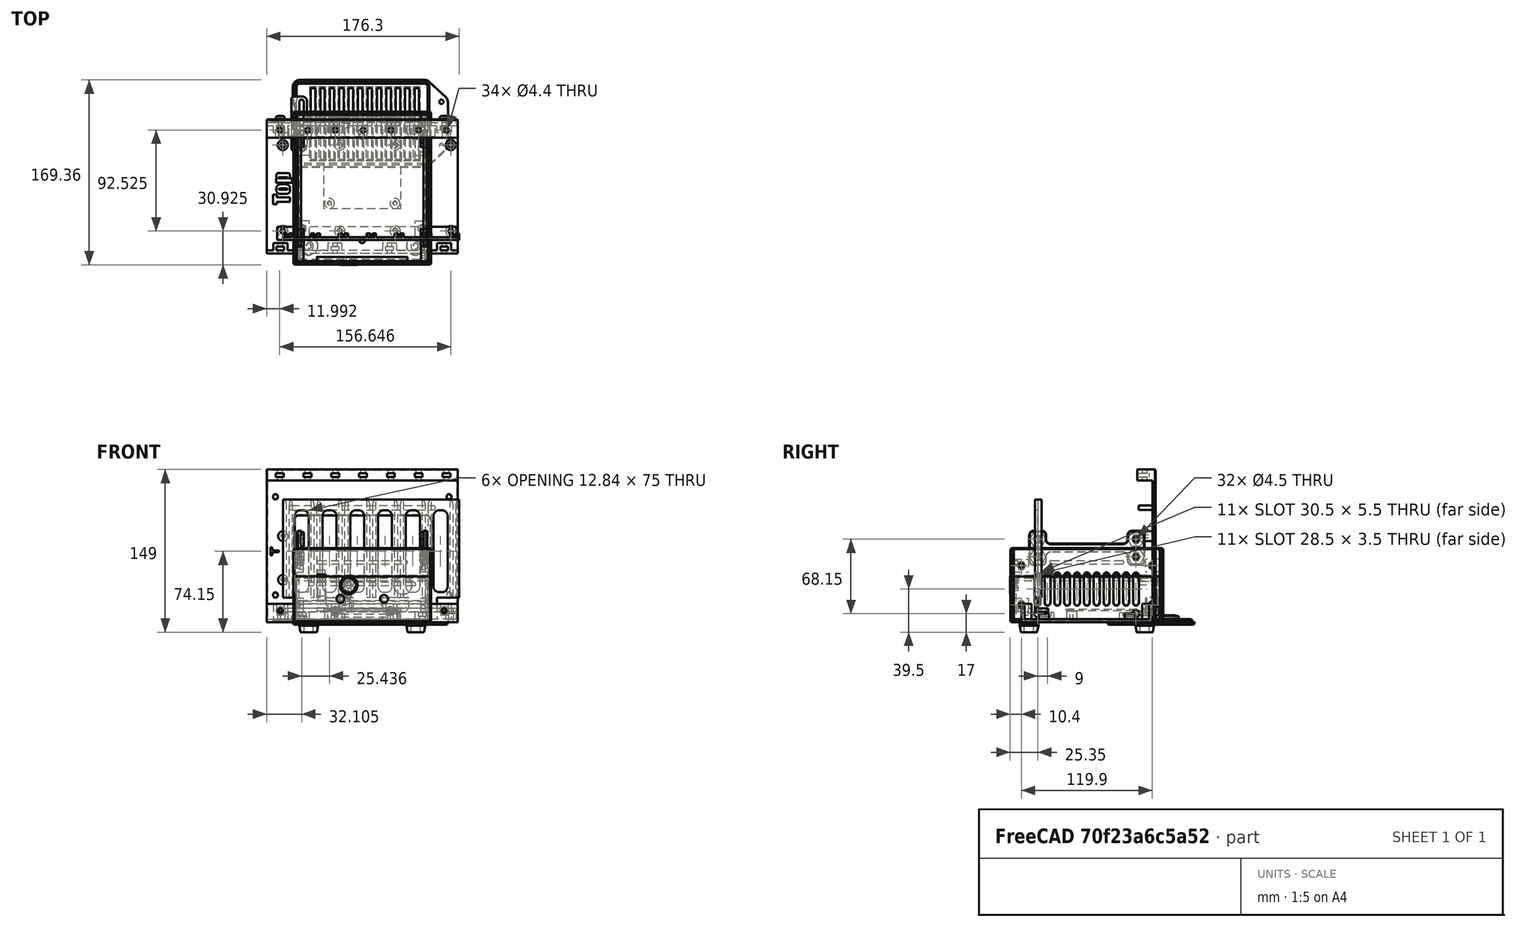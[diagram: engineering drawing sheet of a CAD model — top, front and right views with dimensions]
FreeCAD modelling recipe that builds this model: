
FCSTD DOCUMENT  (FreeCAD 0.19R14555 (Git shallow))
Label: Assembly Model
License: All rights reserved
LicenseURL: http://en.wikipedia.org/wiki/All_rights_reserved
objects: Sketcher::SketchObject×46, PartDesign::Pocket×26, PartDesign::Chamfer×23, PartDesign::Pad×20, PartDesign::Mirrored×12, PartDesign::Body×10, Part::Feature×8, Part::FeaturePython×5, App::Part×5, Part::Mirroring×4, App::DocumentObjectGroup×4, PartDesign::Fillet×4, PartDesign::LinearPattern×1, PartDesign::Revolution×1, PartDesign::Thickness×1, Part::Part2DObjectPython×1
note: 237 computed .brp shape members not serialized (recipe doc carries the construction recipe); baked Part::Feature solids carry a one-line shape summary decoded from their .brp

FEATURE [Part::Feature] Part__Feature001  label="Guide"
  Placement = pos=(4.1875,39.425,9.65) rot=(0,0,1;0rad)
  shape: bbox 166.6 x 12 x 103 mm, 167 faces (baked)
FEATURE [Part::Mirroring] Part__Mirroring001  label="Guide (Mirror #2)"
  Base = (0,0,0)
  Normal = (0,1,0)
  Source = -> Part__Feature001
FEATURE [Part::Feature] Part__Feature004  label="M4 X 10 Pan Hd Pozi"
  Placement = pos=(-75,-63.15,10.5) rot=(1,0,0;1.5708rad)
  shape: bbox 8.444 x 13.1 x 8.444 mm, 27 faces (baked)
FEATURE [Part::FeaturePython] Array  # Draft array (typed FeaturePython)
  Angle = 360
  ArrayType = 0
  Axis = (0,0,1)
  Base = -> Part__Feature004
  Center = (0,0,0)
  Fuse = false
  IntervalAxis = (0,0,0)
  IntervalX = (50,0,0)
  IntervalY = (0,1,0)
  IntervalZ = (0,0,1)
  NumberPolar = 1
  NumberX = 4
  NumberY = 1
  NumberZ = 1
FEATURE [Part::Mirroring] Part__Mirroring003  label="Side panel retaining nuts"
  Base = (0,0,0)
  Normal = (0,1,0)
  Source = -> Array
FEATURE [Part::Feature] Part__Feature005  label="M4 Nut"
  Placement = pos=(-75,-55.375,10.5) rot=(1,0,0;0rad)
  shape: bbox 7.66 x 3.2 x 7.66 mm, 19 faces (baked)
FEATURE [Part::Feature] Part__Feature006  label="Sideplate"
  Placement = pos=(-8e-15,-63.1,0) rot=(0,0.707107,0.707107;3.14159rad)
  shape: bbox 175 x 17 x 140 mm, 120 faces (baked)
FEATURE [Part::Mirroring] Part__Mirroring  label="Sideplate (Mirror #5)"
  Base = (0,0,0)
  Normal = (0,1,0)
  Source = -> Part__Feature006
FEATURE [Part::Feature] Part__Feature007  label="Vented_cover"
  shape: bbox 142 x 80.02 x 8.7 mm, 193 faces (baked)
FEATURE [Part::Feature] Part__Feature008  label="Tab"
  shape: bbox 14.5 x 50 x 2.7 mm, 17 faces (baked)
FEATURE [App::DocumentObjectGroup] Group  label="Side-cover assy"
  Group = -> [Part__Feature007,Part__Feature008]
FEATURE [App::Part] Part  label="Side Cover Assy"
  Group = -> [Part__Feature008,Part__Feature007,Group]
  Origin = -> Origin002
  Placement = pos=(-7.7e-15,-63,0) rot=(0,0.707107,0.707107;3.14159rad)
FEATURE [Part::Feature] Part__Feature009  label="Tab001"
  shape: bbox 14.5 x 50 x 2.7 mm, 17 faces (baked)
FEATURE [Part::Feature] Part__Feature010  label="Vented_cover001"
  shape: bbox 142 x 80.02 x 8.7 mm, 193 faces (baked)
FEATURE [App::DocumentObjectGroup] Group001  label="Side-cover assy001"
  Group = -> [Part__Feature010,Part__Feature009]
FEATURE [App::Part] Part001  label="Side Cover Assy 2"
  Group = -> [Part__Feature009,Part__Feature010,Group001]
  Origin = -> Origin003
  Placement = pos=(7.7e-15,63,118) rot=(0,0.707107,-0.707107;3.14159rad)
FEATURE [Part::FeaturePython] Array001  label="Nuts for sideplate"  # Draft array (typed FeaturePython)
  Angle = 360
  ArrayType = 0
  Axis = (0,0,1)
  Base = -> Part__Feature005
  Center = (0,0,0)
  Fuse = false
  IntervalAxis = (0,0,0)
  IntervalX = (50,0,0)
  IntervalY = (0,1,0)
  IntervalZ = (0,0,1)
  NumberPolar = 1
  NumberX = 4
  NumberY = 1
  NumberZ = 1
FEATURE [Part::Mirroring] Part__Mirroring004  label="Nuts for sideplate (Mirror #5)"
  Base = (0,0,0)
  Normal = (0,1,0)
  Source = -> Array001
FEATURE [Sketcher::SketchObject] Sketch001  label="Base plate spec"
  FullyConstrained = false
  MapMode = 5
  Support = -> [XY_Plane005]
  sketch-geometry (12):
    g0: LineSegment StartX=-63 StartY=67 StartZ=0 EndX=63 EndY=67 EndZ=0
    g1: LineSegment StartX=63 StartY=67 StartZ=0 EndX=63 EndY=-67 EndZ=0
    g2: LineSegment StartX=63 StartY=-67 StartZ=0 EndX=-63 EndY=-67 EndZ=0
    g3: LineSegment StartX=-63 StartY=-67 StartZ=0 EndX=-63 EndY=67 EndZ=0
    g4: Circle CenterX=-49 CenterY=53 CenterZ=0 NormalX=0 NormalY=0 NormalZ=1 AngleXU=0 Radius=2.4
    g5: Circle CenterX=49 CenterY=53 CenterZ=0 NormalX=0 NormalY=0 NormalZ=1 AngleXU=0 Radius=2.4
    g6: Circle CenterX=-49 CenterY=-53 CenterZ=0 NormalX=0 NormalY=0 NormalZ=1 AngleXU=0 Radius=2.4
    g7: Circle CenterX=49 CenterY=-53 CenterZ=0 NormalX=0 NormalY=0 NormalZ=1 AngleXU=0 Radius=2.4
    g8: Circle CenterX=55 CenterY=37 CenterZ=0 NormalX=0 NormalY=0 NormalZ=1 AngleXU=0 Radius=2.4
    g9: Circle CenterX=-55 CenterY=37 CenterZ=0 NormalX=0 NormalY=0 NormalZ=1 AngleXU=0 Radius=2.4
    g10: Circle CenterX=-55 CenterY=-37 CenterZ=0 NormalX=0 NormalY=0 NormalZ=1 AngleXU=0 Radius=2.4
    g11: Circle CenterX=55 CenterY=-37 CenterZ=0 NormalX=0 NormalY=0 NormalZ=1 AngleXU=0 Radius=2.4
  constraints (28):
    c: Coincident(g0,g1)
    c: Coincident(g1,g2)
    c: Coincident(g2,g3)
    c: Coincident(g3,g0)
    c: Horizontal(g2)
    c: Vertical(g1)
    c: Symmetric(g0,g0,g-2)
    c: Symmetric(g0,g2,g-1)
    c: Distance(g0) = 126
    c: Distance(g3) = 134
    c: Radius(g4) = 2.4
    c: Equal(g4,g5)
    c: Equal(g4,g6)
    c: Equal(g4,g7)
    c: Symmetric(g4,g5,g-2)
    c: Symmetric(g4,g6,g-1)
    c: Symmetric(g7,g6,g-2)
    c: Distance(g4,g5) = 98
    c: DistanceY(g6,g4) = 106
    c: Symmetric(g10,g11,g-2)
    c: Symmetric(g9,g10,g-1)
    c: Symmetric(g9,g8,g-2)
    c: Radius(g9) = 2.4
    c: Equal(g9,g8)
    c: Equal(g9,g11)
    c: Equal(g9,g10)
    c: DistanceX(g0,g9) = 8
    c: DistanceY(g9,g0) = 30
FEATURE [PartDesign::Pad] Pad  label="Make base plate"
  AllowMultiFace = false
  Direction = (1,1,1)
  Length = 3
  Length2 = 100
  Profile = -> Sketch001
  Type = 0
FEATURE [Sketcher::SketchObject] Sketch002  label="Sideplate spec"
  FullyConstrained = false
  MapMode = 5
  Placement = pos=(0,0,0) rot=(1,0,0;1.5708rad)
  Support = -> [XZ_Plane006]
  sketch-geometry (4):
    g0: LineSegment StartX=-60 StartY=3.05 StartZ=0 EndX=-63 EndY=3.05 EndZ=0
    g1: LineSegment StartX=-63 StartY=3.05 StartZ=0 EndX=-63 EndY=68.05 EndZ=0
    g2: LineSegment StartX=-63 StartY=68.05 StartZ=0 EndX=-60 EndY=68.05 EndZ=0
    g3: LineSegment StartX=-60 StartY=68.05 StartZ=0 EndX=-60 EndY=3.05 EndZ=0
  constraints (12):
    c: Coincident(g0,g1)
    c: Coincident(g1,g2)
    c: Coincident(g2,g3)
    c: Horizontal(g0)
    c: Horizontal(g2)
    c: Vertical(g3)
    c: Vertical(g1)
    c: Distance(g1) = 65
    c: Distance(g2) = 3
    c: DistanceX(g0) = -63
    c: DistanceY(g0) = 3.05
    c: Coincident(g3,g0)
FEATURE [PartDesign::Pad] Pad001  label="Make sideplate"
  AllowMultiFace = false
  Direction = (1,1,1)
  Length = 134
  Length2 = 100
  Midplane = true
  Placement = pos=(0,0,0) rot=(1,0,0;1.5708rad)
  Profile = -> Sketch002
  Type = 0
FEATURE [Sketcher::SketchObject] Sketch003  label="Screwtab spec"
  ExternalGeometry = -> [Pad001]
  FullyConstrained = false
  MapMode = 5
  Placement = pos=(0,0,3.05) rot=(1,0,0;3.14159rad)
  Support = -> [Pad001]
  sketch-geometry (13):
    g0: LineSegment StartX=-60 StartY=44 StartZ=0 EndX=-48.5 EndY=44 EndZ=0
    g1: LineSegment StartX=-48.5 StartY=44 StartZ=0 EndX=-48.5 EndY=30 EndZ=0
    g2: LineSegment StartX=-48.5 StartY=30 StartZ=0 EndX=-60 EndY=30 EndZ=0
    g3: LineSegment StartX=-60 StartY=30 StartZ=0 EndX=-60 EndY=44 EndZ=0
    g4: LineSegment StartX=-60 StartY=37 StartZ=0 EndX=-48.5 EndY=37 EndZ=0
    g5: Circle CenterX=-55 CenterY=37 CenterZ=0 NormalX=0 NormalY=0 NormalZ=1 AngleXU=0 Radius=2.4
    g6: LineSegment StartX=-51.5 StartY=34.9793 StartZ=0 EndX=-51.5 EndY=39.0207 EndZ=0
    g7: LineSegment StartX=-51.5 StartY=39.0207 StartZ=0 EndX=-55 EndY=41.0415 EndZ=0
    g8: LineSegment StartX=-55 StartY=41.0415 StartZ=0 EndX=-58.5 EndY=39.0207 EndZ=0
    g9: LineSegment StartX=-58.5 StartY=39.0207 StartZ=0 EndX=-58.5 EndY=34.9793 EndZ=0
    g10: LineSegment StartX=-58.5 StartY=34.9793 StartZ=0 EndX=-55 EndY=32.9585 EndZ=0
    g11: LineSegment StartX=-55 StartY=32.9585 StartZ=0 EndX=-51.5 EndY=34.9793 EndZ=0
    g12: Circle CenterX=-55 CenterY=37 CenterZ=0 NormalX=0 NormalY=0 NormalZ=1 AngleXU=0 Radius=4.04145
  constraints (34):
    c: Coincident(g0,g1)
    c: Coincident(g1,g2)
    c: Coincident(g2,g3)
    c: Coincident(g3,g0)
    c: Horizontal(g0)
    c: Horizontal(g2)
    c: Vertical(g1)
    c: Vertical(g3)
    c: Perpendicular(g4,g1) = 4.71239
    c: PointOnObject(g4,g3)
    c: PointOnObject(g5,g4)
    c: PointOnObject(g0,g-3)
    c: Symmetric(g0,g1,g4)
    c: DistanceY(g5,g-3) = 30
    c: DistanceX(g-4,g5) = 8
    c: Coincident(g6,g7)
    c: Coincident(g7,g8)
    c: Coincident(g8,g9)
    c: Coincident(g9,g10)
    c: Coincident(g10,g11)
    c: Coincident(g11,g6)
    c: Equal(g6, g7-g11) x5
    c: PointOnObject(g6,g12)
    c: PointOnObject(g7,g12)
    c: PointOnObject(g8,g12)
    c: PointOnObject(g9,g12)
    c: PointOnObject(g10,g12)
    c: PointOnObject(g11,g12)
    c: Coincident(g12,g5)
    c: Vertical(g6)
    c: DistanceX(g9,g6) = 7
    c: DistanceX(g6,g0) = 3
    c: Distance(g1) = 14
    c: Radius(g5) = 2.4
FEATURE [PartDesign::Pad] Pad002  label="Add screwtab"
  AllowMultiFace = false
  BaseFeature = -> Pad001
  Direction = (1,1,1)
  Length = 6
  Length2 = 100
  Placement = pos=(0,0,0) rot=(1,0,0;1.5708rad)
  Profile = -> Sketch003
  Reversed = true
  Type = 0
FEATURE [PartDesign::Mirrored] Mirrored  label="Mirrored screwtab"
  BaseFeature = -> Pad002
  MirrorPlane = -> XZ_Plane006
  Originals = -> [Pad002]
  Placement = pos=(0,0,0) rot=(1,0,0;1.5708rad)
FEATURE [Sketcher::SketchObject] Sketch004  label="nut trap spec"
  ExternalGeometry = -> [Mirrored]
  FullyConstrained = false
  MapMode = 5
  Placement = pos=(0,-2e-15,9.05) rot=(0,0,1;3.14159rad)
  Support = -> [Mirrored]
  sketch-geometry (7):
    g0: LineSegment StartX=58.55 StartY=34.9504 StartZ=0 EndX=58.55 EndY=39.0496 EndZ=0
    g1: LineSegment StartX=58.55 StartY=39.0496 StartZ=0 EndX=55 EndY=41.0992 EndZ=0
    g2: LineSegment StartX=55 StartY=41.0992 StartZ=0 EndX=51.45 EndY=39.0496 EndZ=0
    g3: LineSegment StartX=51.45 StartY=39.0496 StartZ=0 EndX=51.45 EndY=34.9504 EndZ=0
    g4: LineSegment StartX=51.45 StartY=34.9504 StartZ=0 EndX=55 EndY=32.9008 EndZ=0
    g5: LineSegment StartX=55 StartY=32.9008 StartZ=0 EndX=58.55 EndY=34.9504 EndZ=0
    g6: Circle CenterX=55 CenterY=37 CenterZ=0 NormalX=0 NormalY=0 NormalZ=1 AngleXU=0 Radius=4.09919
  constraints (16):
    c: Coincident(g0,g1)
    c: Coincident(g1,g2)
    c: Coincident(g2,g3)
    c: Coincident(g3,g4)
    c: Coincident(g4,g5)
    c: Coincident(g5,g0)
    c: Equal(g0, g1-g5) x5
    c: PointOnObject(g0,g6)
    c: PointOnObject(g1,g6)
    c: PointOnObject(g2,g6)
    c: PointOnObject(g3,g6)
    c: PointOnObject(g4,g6)
    c: PointOnObject(g5,g6)
    c: Coincident(g6,g-3)
    c: Vertical(g0)
    c: Distance(g0,g3) = 7.1
FEATURE [PartDesign::Pocket] Pocket  label="Add nut trap"
  AllowMultiFace = false
  BaseFeature = -> Mirrored
  Length = 3.5
  Length2 = 100
  Placement = pos=(0,0,0) rot=(1,0,0;1.5708rad)
  Profile = -> Sketch004
  Type = 0
FEATURE [PartDesign::Mirrored] Mirrored001  label="Mirrored nut-trap"
  BaseFeature = -> Pocket
  MirrorPlane = -> XZ_Plane006
  Originals = -> [Pocket]
  Placement = pos=(0,0,0) rot=(1,0,0;1.5708rad)
FEATURE [Sketcher::SketchObject] Sketch005  label="PCB Base"
  FullyConstrained = false
  MapMode = 5
  Support = -> [XY_Plane007]
  sketch-geometry (11):
    g0: LineSegment StartX=-50 StartY=35 StartZ=0 EndX=35 EndY=35 EndZ=0
    g1: LineSegment StartX=35 StartY=35 StartZ=0 EndX=35 EndY=-35 EndZ=0
    g2: LineSegment StartX=35 StartY=-35 StartZ=0 EndX=-50 EndY=-35 EndZ=0
    g3: LineSegment StartX=-50 StartY=-35 StartZ=0 EndX=-50 EndY=35 EndZ=0
    g4: Circle CenterX=-45 CenterY=-30 CenterZ=0 NormalX=0 NormalY=0 NormalZ=1 AngleXU=0 Radius=2.1
    g5: Circle CenterX=30 CenterY=-30 CenterZ=0 NormalX=0 NormalY=0 NormalZ=1 AngleXU=0 Radius=2.1
    g6: Circle CenterX=-45 CenterY=30 CenterZ=0 NormalX=0 NormalY=0 NormalZ=1 AngleXU=0 Radius=2.1
    g7: Circle CenterX=30 CenterY=30 CenterZ=0 NormalX=0 NormalY=0 NormalZ=1 AngleXU=0 Radius=2.1
    g8: LineSegment StartX=-7.5 StartY=35 StartZ=0 EndX=-7.5 EndY=-35 EndZ=0
    g9: LineSegment StartX=-50 StartY=-3.1e-15 StartZ=0 EndX=35 EndY=2.1e-15 EndZ=0
    g10: GeomPoint X=0 Y=0 Z=0
  constraints (28):
    c: Coincident(g0,g1)
    c: Coincident(g1,g2)
    c: Coincident(g2,g3)
    c: Coincident(g3,g0)
    c: Horizontal(g0)
    c: Horizontal(g2)
    c: Vertical(g1)
    c: Vertical(g3)
    c: Distance(g3) = 70
    c: Distance(g0) = 85
    c: Radius(g6) = 2.1
    c: Equal(g6,g7)
    c: Equal(g6,g4)
    c: Equal(g6,g5)
    c: Perpendicular(g9,g3) = 1.5708
    c: Perpendicular(g8,g0) = 1.5708
    c: PointOnObject(g8,g2)
    c: PointOnObject(g9,g1)
    c: Symmetric(g2,g0,g9)
    c: Symmetric(g0,g0,g8)
    c: Symmetric(g6,g7,g8)
    c: Symmetric(g4,g6,g9)
    c: Symmetric(g4,g5,g8)
    c: DistanceX(g2,g4) = 5
    c: DistanceY(g2,g4) = 5
    c: Coincident(g10,g-1)
    c: PointOnObject(g10,g9)
    c: DistanceX(g0) = 35
FEATURE [PartDesign::Pad] Pad003  label="Make PCB Laminate"
  AllowMultiFace = false
  Direction = (1,1,1)
  Length = 1.6
  Length2 = 100
  Profile = -> Sketch005
  Type = 0
FEATURE [Sketcher::SketchObject] Sketch006  label="DCJack footprint"
  ExternalGeometry = -> [Pad003]
  FullyConstrained = false
  MapMode = 5
  Placement = pos=(0,0,1.6) rot=(0,0,1;0rad)
  Support = -> [Pad003]
  sketch-geometry (7):
    g0: LineSegment StartX=23.95 StartY=20.45 StartZ=0 EndX=38 EndY=20.45 EndZ=0
    g1: LineSegment StartX=38 StartY=20.45 StartZ=0 EndX=38 EndY=11.45 EndZ=0
    g2: LineSegment StartX=38 StartY=11.45 StartZ=0 EndX=23.95 EndY=11.45 EndZ=0
    g3: LineSegment StartX=23.95 StartY=11.45 StartZ=0 EndX=23.95 EndY=20.45 EndZ=0
    g4: LineSegment StartX=38 StartY=15.95 StartZ=0 EndX=23.95 EndY=15.95 EndZ=0
    g5: LineSegment StartX=30.975 StartY=20.45 StartZ=0 EndX=30.975 EndY=11.45 EndZ=0
    g6: GeomPoint X=30.975 Y=15.95 Z=0
  constraints (19):
    c: Coincident(g0,g1)
    c: Coincident(g1,g2)
    c: Coincident(g2,g3)
    c: Coincident(g3,g0)
    c: Horizontal(g0)
    c: Horizontal(g2)
    c: Vertical(g1)
    c: Distance(g1) = 9
    c: Distance(g2) = 14.05
    c: Perpendicular(g4,g1) = 1.5708
    c: PointOnObject(g4,g3)
    c: Perpendicular(g5,g0) = 1.5708
    c: PointOnObject(g5,g2)
    c: Symmetric(g0,g0,g5)
    c: Symmetric(g2,g0,g4)
    c: PointOnObject(g6,g5)
    c: PointOnObject(g6,g4)
    c: DistanceY(g6,g-3) = 19.05
    c: DistanceX(g-3,g0) = 3
FEATURE [PartDesign::Pad] Pad004  label="DC Jack block"
  AllowMultiFace = false
  BaseFeature = -> Pad003
  Direction = (1,1,1)
  Length = 11
  Length2 = 100
  Profile = -> Sketch006
  Type = 0
FEATURE [Sketcher::SketchObject] Sketch007  label="hole and pin spec"
  ExternalGeometry = -> [Pad004]
  FullyConstrained = false
  MapMode = 5
  Placement = pos=(38,0,0) rot=(0.57735,0.57735,0.57735;2.0944rad)
  Support = -> [Pad004]
  sketch-geometry (3):
    g0: Circle CenterX=15.95 CenterY=8.1 CenterZ=0 NormalX=0 NormalY=0 NormalZ=1 AngleXU=0 Radius=3.25
    g1: LineSegment StartX=15.95 StartY=12.6 StartZ=0 EndX=15.95 EndY=11.35 EndZ=0
    g2: Circle CenterX=15.95 CenterY=8.1 CenterZ=0 NormalX=0 NormalY=0 NormalZ=1 AngleXU=0 Radius=1.05
  constraints (7):
    c: Perpendicular(g1,g0) = 4.71239
    c: Perpendicular(g1,g-3) = 4.71239
    c: Symmetric(g-3,g-3,g1)
    c: Radius(g0) = 3.25
    c: Distance(g1) = 1.25
    c: Coincident(g2,g0)
    c: Radius(g2) = 1.05
FEATURE [PartDesign::Pocket] Pocket001  label="Make hole and pin spec"
  AllowMultiFace = false
  BaseFeature = -> Pad004
  Length = 9.5
  Length2 = 100
  Profile = -> Sketch007
  Type = 0
FEATURE [PartDesign::Fillet] Fillet001  label="Finish pin"
  Base = -> Pocket001 [Edge46]
  BaseFeature = -> Pocket001
  Radius = 0.5
  SupportTransform = false
FEATURE [Sketcher::SketchObject] Sketch008  label="Unneccesary back face decor"
  ExternalGeometry = -> [Fillet001]
  FullyConstrained = false
  MapMode = 5
  Placement = pos=(23.95,0,0) rot=(0.57735,-0.57735,-0.57735;2.0944rad)
  Support = -> [Fillet001]
  sketch-geometry (5):
    g0: ArcOfCircle CenterX=-15.95 CenterY=7.95 CenterZ=0 NormalX=0 NormalY=0 NormalZ=1 AngleXU=0 Radius=4.5 StartAngle=0 EndAngle=3.14159
    g1: LineSegment StartX=-20.45 StartY=7.95 StartZ=0 EndX=-20.45 EndY=12.6 EndZ=0
    g2: LineSegment StartX=-20.45 StartY=12.6 StartZ=0 EndX=-11.45 EndY=12.6 EndZ=0
    g3: LineSegment StartX=-11.45 StartY=12.6 StartZ=0 EndX=-11.45 EndY=7.95 EndZ=0
    g4: LineSegment StartX=-15.95 StartY=12.45 StartZ=0 EndX=-15.95 EndY=12.6 EndZ=0
  constraints (11):
    c: Coincident(g1,g2)
    c: Coincident(g2,g3)
    c: Vertical(g3)
    c: Vertical(g1)
    c: Coincident(g1,g-5)
    c: Coincident(g2,g-4)
    c: Tangent(g0,g3) = 1.5708
    c: Tangent(g1,g0) = 1.5708
    c: Perpendicular(g4,g2) = 4.71239
    c: Perpendicular(g4,g0) = 1.5708
    c: Distance(g4) = 0.15
FEATURE [PartDesign::Pocket] Pocket002  label="Add jack back decor"
  AllowMultiFace = false
  BaseFeature = -> Fillet001
  Length = 10
  Length2 = 100
  Profile = -> Sketch008
  Type = 0
FEATURE [PartDesign::Body] Body003  label="PCB"
  Group = -> [Sketch005,Pad003,Sketch006,Pad004,Sketch007,Pocket001,Fillet001,Sketch008,Pocket002]
  Origin = -> Origin007
  Placement = pos=(0,31,10.6) rot=(0,0,1;1.5708rad)
  Tip = -> Pocket002
FEATURE [Sketcher::SketchObject] Sketch009  label="PCB Mounting pillar spec"
  FullyConstrained = false
  MapMode = 5
  Placement = pos=(0,0,3) rot=(0,0,1;0rad)
  Support = -> [Pad]
  sketch-geometry (10):
    g0: LineSegment StartX=-30 StartY=61 StartZ=0 EndX=30 EndY=61 EndZ=0
    g1: LineSegment StartX=30 StartY=61 StartZ=0 EndX=30 EndY=-14 EndZ=0
    g2: LineSegment StartX=30 StartY=-14 StartZ=0 EndX=-30 EndY=-14 EndZ=0
    g3: LineSegment StartX=-30 StartY=-14 StartZ=0 EndX=-30 EndY=61 EndZ=0
    g4: Circle CenterX=-30 CenterY=61 CenterZ=0 NormalX=0 NormalY=0 NormalZ=1 AngleXU=0 Radius=4.5
    g5: Circle CenterX=30 CenterY=61 CenterZ=0 NormalX=0 NormalY=0 NormalZ=1 AngleXU=0 Radius=4.5
    g6: Circle CenterX=-30 CenterY=-14 CenterZ=0 NormalX=0 NormalY=0 NormalZ=1 AngleXU=0 Radius=4.5
    g7: Circle CenterX=30 CenterY=-14 CenterZ=0 NormalX=0 NormalY=0 NormalZ=1 AngleXU=0 Radius=4.5
    g8: LineSegment StartX=-2.3e-15 StartY=61 StartZ=0 EndX=2.3e-15 EndY=-14 EndZ=0
    g9: LineSegment StartX=-30 StartY=23.5 StartZ=0 EndX=0 EndY=23.5 EndZ=0
  constraints (26):
    c: Coincident(g0,g1)
    c: Coincident(g1,g2)
    c: Coincident(g2,g3)
    c: Coincident(g3,g0)
    c: Horizontal(g0)
    c: Horizontal(g2)
    c: Vertical(g1)
    c: Vertical(g3)
    c: Distance(g0) = 60
    c: Distance(g3) = 75
    c: Coincident(g6,g2)
    c: Coincident(g7,g1)
    c: Coincident(g5,g0)
    c: Coincident(g4,g0)
    c: Radius(g4) = 4.5
    c: Equal(g4,g5)
    c: Equal(g4,g7)
    c: Equal(g4,g6)
    c: Perpendicular(g9,g3) = 1.5708
    c: Perpendicular(g8,g0) = 1.5708
    c: PointOnObject(g9,g8)
    c: PointOnObject(g8,g2)
    c: Symmetric(g5,g4,g8)
    c: Symmetric(g6,g4,g9)
    c: PointOnObject(g9,g-2)
    c: DistanceY(g4) = 61
FEATURE [PartDesign::Pad] Pad005  label="Add PCB Mounting pillars 7.4 high"
  AllowMultiFace = false
  BaseFeature = -> Pad
  Direction = (1,1,1)
  Length = 7.4
  Length2 = 100
  Profile = -> Sketch009
  Type = 0
FEATURE [Sketcher::SketchObject] Sketch010  label="PCB Screwhole spec"
  ExternalGeometry = -> [Pad005]
  FullyConstrained = false
  MapMode = 5
  Placement = pos=(0,0,10.4) rot=(0,0,1;0rad)
  Support = -> [Pad005]
  sketch-geometry (4):
    g0: Circle CenterX=-30 CenterY=61 CenterZ=0 NormalX=0 NormalY=0 NormalZ=1 AngleXU=0 Radius=1.5
    g1: Circle CenterX=30 CenterY=61 CenterZ=0 NormalX=0 NormalY=0 NormalZ=1 AngleXU=0 Radius=1.5
    g2: Circle CenterX=30 CenterY=-14 CenterZ=0 NormalX=0 NormalY=0 NormalZ=1 AngleXU=0 Radius=1.5
    g3: Circle CenterX=-30 CenterY=-14 CenterZ=0 NormalX=0 NormalY=0 NormalZ=1 AngleXU=0 Radius=1.5
  constraints (8):
    c: Radius(g0) = 1.5
    c: Equal(g0,g1)
    c: Equal(g0,g2)
    c: Equal(g0,g3)
    c: Coincident(g3,g-6)
    c: Coincident(g2,g-5)
    c: Coincident(g0,g-3)
    c: Coincident(g1,g-4)
FEATURE [Sketcher::SketchObject] Sketch011  label="Front Endplate spec"
  FullyConstrained = false
  MapMode = 5
  Placement = pos=(0,0,0) rot=(1,0,0;1.5708rad)
  Support = -> [XZ_Plane008]
  sketch-geometry (4):
    g0: LineSegment StartX=-63 StartY=68 StartZ=0 EndX=63 EndY=68 EndZ=0
    g1: LineSegment StartX=63 StartY=68 StartZ=0 EndX=63 EndY=0 EndZ=0
    g2: LineSegment StartX=63 StartY=0 StartZ=0 EndX=-63 EndY=0 EndZ=0
    g3: LineSegment StartX=-63 StartY=0 StartZ=0 EndX=-63 EndY=68 EndZ=0
  constraints (11):
    c: Coincident(g0,g1)
    c: Coincident(g1,g2)
    c: Coincident(g2,g3)
    c: Coincident(g3,g0)
    c: Horizontal(g2)
    c: Vertical(g1)
    c: Vertical(g3)
    c: Distance(g0) = 126
    c: Symmetric(g0,g0,g-2)
    c: Distance(g3) = 68
    c: PointOnObject(g2,g-1)
FEATURE [PartDesign::Pad] Pad006  label="Make front endplate"
  AllowMultiFace = false
  Direction = (1,1,1)
  Length = 3
  Length2 = 100
  Placement = pos=(0,0,0) rot=(1,0,0;1.5708rad)
  Profile = -> Sketch011
  Type = 0
FEATURE [Sketcher::SketchObject] Sketch012  label="Endplate mounting blocks"
  ExternalGeometry = -> [Pad006]
  FullyConstrained = false
  MapMode = 5
  Placement = pos=(0,-1e-16,0) rot=(-1,0,0;1.5708rad)
  Support = -> [Pad006]
  sketch-geometry (9):
    g0: LineSegment StartX=-59.85 StartY=-10 StartZ=0 EndX=-53.85 EndY=-10 EndZ=0
    g1: LineSegment StartX=-53.85 StartY=-10 StartZ=0 EndX=-53.85 EndY=-22 EndZ=0
    g2: LineSegment StartX=-53.85 StartY=-22 StartZ=0 EndX=-59.85 EndY=-22 EndZ=0
    g3: LineSegment StartX=-59.85 StartY=-22 StartZ=0 EndX=-59.85 EndY=-10 EndZ=0
    g4: LineSegment StartX=-59.85 StartY=-46 StartZ=0 EndX=-53.85 EndY=-46 EndZ=0
    g5: LineSegment StartX=-53.85 StartY=-46 StartZ=0 EndX=-53.85 EndY=-58 EndZ=0
    g6: LineSegment StartX=-53.85 StartY=-58 StartZ=0 EndX=-59.85 EndY=-58 EndZ=0
    g7: LineSegment StartX=-59.85 StartY=-58 StartZ=0 EndX=-59.85 EndY=-46 EndZ=0
    g8: LineSegment StartX=-59.85 StartY=-22 StartZ=0 EndX=-59.85 EndY=-46 EndZ=0
  constraints (26):
    c: Coincident(g0,g1)
    c: Coincident(g1,g2)
    c: Coincident(g2,g3)
    c: Coincident(g3,g0)
    c: Horizontal(g0)
    c: Horizontal(g2)
    c: Vertical(g1)
    c: Vertical(g3)
    c: Coincident(g4,g5)
    c: Coincident(g5,g6)
    c: Coincident(g6,g7)
    c: Coincident(g7,g4)
    c: Horizontal(g4)
    c: Horizontal(g6)
    c: Vertical(g5)
    c: Vertical(g7)
    c: Equal(g0,g4)
    c: Equal(g5,g1)
    c: Distance(g0) = 6
    c: DistanceY(g0) = -10
    c: DistanceY(g-3,g6) = 10
    c: DistanceX(g-3,g6) = 3.15
    c: Coincident(g4,g8)
    c: Vertical(g8)
    c: Coincident(g8,g2)
    c: Distance(g1) = 12
FEATURE [PartDesign::Pad] Pad007
  AllowMultiFace = false
  BaseFeature = -> Pad006
  Direction = (1,1,1)
  Length = 13.5
  Length2 = 100
  Placement = pos=(0,0,0) rot=(1,0,0;1.5708rad)
  Profile = -> Sketch012
  Type = 0
FEATURE [PartDesign::Mirrored] Mirrored002
  BaseFeature = -> Pad007
  MirrorPlane = -> YZ_Plane008
  Originals = -> [Pad007]
  Placement = pos=(0,0,0) rot=(1,0,0;1.5708rad)
FEATURE [Sketcher::SketchObject] Sketch013  label="Side mounting hole spec"
  ExternalGeometry = -> [Mirrored002]
  FullyConstrained = false
  MapMode = 5
  Placement = pos=(59.85,-1.32e-14,1.32e-14) rot=(0.707107,0,0.707107;3.14159rad)
  Support = -> [Mirrored002]
  sketch-geometry (6):
    g0: Circle CenterX=16 CenterY=-7 CenterZ=0 NormalX=0 NormalY=0 NormalZ=1 AngleXU=0 Radius=2.25
    g1: Circle CenterX=52 CenterY=-7 CenterZ=0 NormalX=0 NormalY=0 NormalZ=1 AngleXU=0 Radius=2.25
    g2: LineSegment StartX=52 StartY=-7 StartZ=0 EndX=52 EndY=-13.5 EndZ=0
    g3: LineSegment StartX=52 StartY=-7 StartZ=0 EndX=58 EndY=-7 EndZ=0
    g4: LineSegment StartX=52 StartY=-7 StartZ=0 EndX=16 EndY=-7 EndZ=0
    g5: LineSegment StartX=16 StartY=-7 StartZ=0 EndX=16 EndY=-13.5 EndZ=0
  constraints (15):
    c: Coincident(g2,g1)
    c: Coincident(g2,g3)
    c: Horizontal(g3)
    c: PointOnObject(g2,g-5)
    c: Symmetric(g-6,g-5,g2)
    c: PointOnObject(g3,g-6)
    c: DistanceY(g3,g-6) = 7
    c: Coincident(g4,g1)
    c: Coincident(g4,g0)
    c: Horizontal(g4)
    c: Coincident(g5,g0)
    c: Perpendicular(g5,g-3) = 4.71239
    c: Symmetric(g-3,g-4,g5)
    c: Radius(g0) = 2.25
    c: Equal(g0,g1)
FEATURE [PartDesign::Pocket] Pocket004  label="Add side mounting holes001"
  AllowMultiFace = false
  BaseFeature = -> Mirrored002
  Length = 5
  Length2 = 100
  Placement = pos=(0,0,0) rot=(1,0,0;1.5708rad)
  Profile = -> Sketch013
  Type = 1
FEATURE [Sketcher::SketchObject] Sketch014  label="Nut trap spec"
  ExternalGeometry = -> [Pocket004]
  FullyConstrained = false
  MapMode = 5
  Placement = pos=(-53.85,0,0) rot=(0.707107,0,0.707107;3.14159rad)
  Support = -> [Pocket004]
  sketch-geometry (14):
    g0: LineSegment StartX=19.5 StartY=-9.02073 StartZ=0 EndX=19.5 EndY=-4.97927 EndZ=0
    g1: LineSegment StartX=19.5 StartY=-4.97927 StartZ=0 EndX=16 EndY=-2.95855 EndZ=0
    g2: LineSegment StartX=16 StartY=-2.95855 StartZ=0 EndX=12.5 EndY=-4.97927 EndZ=0
    g3: LineSegment StartX=12.5 StartY=-4.97927 StartZ=0 EndX=12.5 EndY=-9.02073 EndZ=0
    g4: LineSegment StartX=12.5 StartY=-9.02073 StartZ=0 EndX=16 EndY=-11.0415 EndZ=0
    g5: LineSegment StartX=16 StartY=-11.0415 StartZ=0 EndX=19.5 EndY=-9.02073 EndZ=0
    g6: Circle CenterX=16 CenterY=-7 CenterZ=0 NormalX=0 NormalY=0 NormalZ=1 AngleXU=0 Radius=4.04145
    g7: LineSegment StartX=55.5 StartY=-9.02073 StartZ=0 EndX=55.5 EndY=-4.97927 EndZ=0
    g8: LineSegment StartX=55.5 StartY=-4.97927 StartZ=0 EndX=52 EndY=-2.95855 EndZ=0
    g9: LineSegment StartX=52 StartY=-2.95855 StartZ=0 EndX=48.5 EndY=-4.97927 EndZ=0
    g10: LineSegment StartX=48.5 StartY=-4.97927 StartZ=0 EndX=48.5 EndY=-9.02073 EndZ=0
    g11: LineSegment StartX=48.5 StartY=-9.02073 StartZ=0 EndX=52 EndY=-11.0415 EndZ=0
    g12: LineSegment StartX=52 StartY=-11.0415 StartZ=0 EndX=55.5 EndY=-9.02073 EndZ=0
    g13: Circle CenterX=52 CenterY=-7 CenterZ=0 NormalX=0 NormalY=0 NormalZ=1 AngleXU=0 Radius=4.04145
  constraints (32):
    c: Coincident(g0,g1)
    c: Coincident(g1,g2)
    c: Coincident(g2,g3)
    c: Coincident(g3,g4)
    c: Coincident(g4,g5)
    c: Coincident(g5,g0)
    c: Equal(g0, g1-g5) x5
    c: PointOnObject(g0,g6)
    c: PointOnObject(g1,g6)
    c: PointOnObject(g2,g6)
    c: PointOnObject(g3,g6)
    c: PointOnObject(g4,g6)
    c: PointOnObject(g5,g6)
    c: Coincident(g7,g8)
    c: Coincident(g8,g9)
    c: Coincident(g9,g10)
    c: Coincident(g10,g11)
    c: Coincident(g11,g12)
    c: Coincident(g12,g7)
    c: Equal(g7, g8-g12) x5
    c: PointOnObject(g7,g13)
    c: PointOnObject(g8,g13)
    c: PointOnObject(g9,g13)
    c: PointOnObject(g10,g13)
    c: PointOnObject(g11,g13)
    c: PointOnObject(g12,g13)
    c: Vertical(g0)
    c: Vertical(g7)
    c: Coincident(g6,g-3)
    c: Coincident(g13,g-4)
    c: Distance(g2,g0) = 7
    c: Equal(g13,g6)
FEATURE [PartDesign::Pocket] Pocket005  label="Add nut trap to side mounting lugs"
  AllowMultiFace = false
  BaseFeature = -> Pocket004
  Length = 3.5
  Length2 = 100
  Placement = pos=(0,0,0) rot=(1,0,0;1.5708rad)
  Profile = -> Sketch014
  Type = 0
FEATURE [Sketcher::SketchObject] Sketch015  label="Side mounting screwhole spec one end"
  ExternalGeometry = -> [Mirrored001]
  FullyConstrained = false
  MapMode = 5
  Placement = pos=(-63,0,0) rot=(0.707107,0,-0.707107;3.14159rad)
  Support = -> [Mirrored001]
  sketch-geometry (3):
    g0: Circle CenterX=-16 CenterY=59.9 CenterZ=0 NormalX=0 NormalY=0 NormalZ=1 AngleXU=0 Radius=2.25
    g1: Circle CenterX=-52.05 CenterY=59.9 CenterZ=0 NormalX=0 NormalY=0 NormalZ=1 AngleXU=0 Radius=2.25
    g2: LineSegment StartX=-52.05 StartY=59.9 StartZ=0 EndX=-16 EndY=59.9 EndZ=0
  constraints (8):
    c: Radius(g1) = 2.25
    c: Equal(g1,g0)
    c: Horizontal(g2)
    c: Coincident(g2,g1)
    c: Coincident(g2,g0)
    c: DistanceX(g0,g-3) = 12.95
    c: DistanceX(g-3,g1) = 16
    c: DistanceY(g0,g-3) = 7.1
FEATURE [PartDesign::Pocket] Pocket006  label="Add one end side-mounting screwholes"
  AllowMultiFace = false
  BaseFeature = -> Mirrored001
  Length = 5
  Length2 = 100
  Placement = pos=(0,0,0) rot=(1,0,0;1.5708rad)
  Profile = -> Sketch015
  Type = 1
FEATURE [PartDesign::Mirrored] Mirrored003  label="side mounting holes Mirrored"
  BaseFeature = -> Pocket006
  MirrorPlane = -> XZ_Plane006
  Originals = -> [Pocket006]
  Placement = pos=(0,0,0) rot=(1,0,0;1.5708rad)
FEATURE [Sketcher::SketchObject] Sketch016  label="Base to main-box interface hole spec"
  ExternalGeometry = -> [Mirrored003]
  FullyConstrained = false
  MapMode = 5
  Placement = pos=(-60,0,0) rot=(0.707107,0,0.707107;3.14159rad)
  Support = -> [Mirrored003]
  sketch-geometry (2):
    g0: Circle CenterX=60.05 CenterY=45 CenterZ=0 NormalX=0 NormalY=0 NormalZ=1 AngleXU=0 Radius=2.25
    g1: Circle CenterX=60.05 CenterY=-45 CenterZ=0 NormalX=0 NormalY=0 NormalZ=1 AngleXU=0 Radius=2.25
  constraints (5):
    c: Symmetric(g1,g0,g-1)
    c: Radius(g0) = 2.25
    c: Equal(g0,g1)
    c: DistanceY(g0,g-3) = 22
    c: DistanceX(g0,g-3) = 8
FEATURE [PartDesign::Pocket] Pocket007  label="Base to mainbox interface holes"
  AllowMultiFace = false
  BaseFeature = -> Mirrored003
  Length = 5
  Length2 = 100
  Placement = pos=(0,0,0) rot=(1,0,0;1.5708rad)
  Profile = -> Sketch016
  Type = 1
FEATURE [Sketcher::SketchObject] Sketch017  label="Grille slot"
  FullyConstrained = false
  MapMode = 5
  Placement = pos=(-63,0,0) rot=(0.707107,0,-0.707107;3.14159rad)
  Support = -> [Pocket007]
  sketch-geometry (4):
    g0: ArcOfCircle CenterX=-43 CenterY=45 CenterZ=0 NormalX=0 NormalY=0 NormalZ=1 AngleXU=0 Radius=1.75 StartAngle=1.5708 EndAngle=4.71239
    g1: ArcOfCircle CenterX=-18 CenterY=45 CenterZ=0 NormalX=0 NormalY=0 NormalZ=1 AngleXU=0 Radius=1.75 StartAngle=4.71239 EndAngle=7.85398
    g2: LineSegment StartX=-43 StartY=43.25 StartZ=0 EndX=-18 EndY=43.25 EndZ=0
    g3: LineSegment StartX=-43 StartY=46.75 StartZ=0 EndX=-18 EndY=46.75 EndZ=0
  constraints (10):
    c: Tangent(g0,g3) = 1.5708
    c: Tangent(g0,g2) = -1.5708
    c: Tangent(g2,g1) = -1.5708
    c: Tangent(g3,g1) = 1.5708
    c: Equal(g0,g1)
    c: Distance(g0,g0) = 3.5
    c: Distance(g3) = 25
    c: DistanceX(g1) = -18
    c: DistanceY(g1) = 45
    c: Horizontal(g3)
FEATURE [PartDesign::Pocket] Pocket008  label="Add grille slot"
  AllowMultiFace = false
  BaseFeature = -> Pocket007
  Length = 5
  Length2 = 100
  Placement = pos=(0,0,0) rot=(1,0,0;1.5708rad)
  Profile = -> Sketch017
  Type = 1
FEATURE [PartDesign::LinearPattern] LinearPattern  label="Make grille pattern"
  BaseFeature = -> Pocket008
  Direction = -> Sketch017 [V_Axis]
  Length = 90
  Occurrences = 11
  Originals = -> [Pocket008]
  Placement = pos=(0,0,0) rot=(1,0,0;1.5708rad)
  Reversed = true
FEATURE [PartDesign::Chamfer] Chamfer001  label="Grille Chamfer"
  Angle = 45
  Base = -> LinearPattern [Edge106,Edge103,Edge97,Edge93,Edge85,Edge89,Edge81,Edge125,Edge121,Edge112,Edge116]
  BaseFeature = -> LinearPattern
  ChamferType = 0
  FlipDirection = false
  Placement = pos=(0,0,0) rot=(1,0,0;1.5708rad)
  Size = 1
  Size2 = 1
  SupportTransform = false
FEATURE [Sketcher::SketchObject] Sketch018  label="Rear endplate spec"
  FullyConstrained = false
  MapMode = 5
  Placement = pos=(0,0,0) rot=(1,0,0;1.5708rad)
  Support = -> [XZ_Plane009]
  sketch-geometry (4):
    g0: LineSegment StartX=-63 StartY=68 StartZ=0 EndX=63 EndY=68 EndZ=0
    g1: LineSegment StartX=63 StartY=68 StartZ=0 EndX=63 EndY=0 EndZ=0
    g2: LineSegment StartX=63 StartY=0 StartZ=0 EndX=-63 EndY=0 EndZ=0
    g3: LineSegment StartX=-63 StartY=0 StartZ=0 EndX=-63 EndY=68 EndZ=0
  constraints (11):
    c: Coincident(g0,g1)
    c: Coincident(g1,g2)
    c: Coincident(g2,g3)
    c: Coincident(g3,g0)
    c: Horizontal(g2)
    c: Vertical(g1)
    c: Vertical(g3)
    c: Distance(g0) = 126
    c: Symmetric(g0,g0,g-2)
    c: Distance(g3) = 68
    c: PointOnObject(g2,g-1)
FEATURE [PartDesign::Pad] Pad008  label="Make rear endplate"
  AllowMultiFace = false
  Direction = (1,1,1)
  Length = 3
  Length2 = 100
  Placement = pos=(0,0,0) rot=(1,0,0;1.5708rad)
  Profile = -> Sketch018
  Type = 0
FEATURE [Sketcher::SketchObject] Sketch019  label="Rear endplate mounting blocks"
  ExternalGeometry = -> [Pad008]
  FullyConstrained = false
  MapMode = 5
  Placement = pos=(0,-1e-16,0) rot=(-1,0,0;1.5708rad)
  Support = -> [Pad008]
  sketch-geometry (9):
    g0: LineSegment StartX=-59.85 StartY=-10 StartZ=0 EndX=-53.85 EndY=-10 EndZ=0
    g1: LineSegment StartX=-53.85 StartY=-10 StartZ=0 EndX=-53.85 EndY=-22 EndZ=0
    g2: LineSegment StartX=-53.85 StartY=-22 StartZ=0 EndX=-59.85 EndY=-22 EndZ=0
    g3: LineSegment StartX=-59.85 StartY=-22 StartZ=0 EndX=-59.85 EndY=-10 EndZ=0
    g4: LineSegment StartX=-59.85 StartY=-46 StartZ=0 EndX=-53.85 EndY=-46 EndZ=0
    g5: LineSegment StartX=-53.85 StartY=-46 StartZ=0 EndX=-53.85 EndY=-58 EndZ=0
    g6: LineSegment StartX=-53.85 StartY=-58 StartZ=0 EndX=-59.85 EndY=-58 EndZ=0
    g7: LineSegment StartX=-59.85 StartY=-58 StartZ=0 EndX=-59.85 EndY=-46 EndZ=0
    g8: LineSegment StartX=-59.85 StartY=-22 StartZ=0 EndX=-59.85 EndY=-46 EndZ=0
  constraints (26):
    c: Coincident(g0,g1)
    c: Coincident(g1,g2)
    c: Coincident(g2,g3)
    c: Coincident(g3,g0)
    c: Horizontal(g0)
    c: Horizontal(g2)
    c: Vertical(g1)
    c: Vertical(g3)
    c: Coincident(g4,g5)
    c: Coincident(g5,g6)
    c: Coincident(g6,g7)
    c: Coincident(g7,g4)
    c: Horizontal(g4)
    c: Horizontal(g6)
    c: Vertical(g5)
    c: Vertical(g7)
    c: Equal(g0,g4)
    c: Equal(g5,g1)
    c: Distance(g0) = 6
    c: DistanceY(g0) = -10
    c: DistanceY(g-3,g6) = 10
    c: DistanceX(g-3,g6) = 3.15
    c: Coincident(g4,g8)
    c: Vertical(g8)
    c: Coincident(g8,g2)
    c: Distance(g1) = 12
FEATURE [PartDesign::Pad] Pad009  label="Add rear endplate mounting blocks"
  AllowMultiFace = false
  BaseFeature = -> Pad008
  Direction = (1,1,1)
  Length = 13.5
  Length2 = 100
  Placement = pos=(0,0,0) rot=(1,0,0;1.5708rad)
  Profile = -> Sketch019
  Type = 0
FEATURE [PartDesign::Mirrored] Mirrored004
  BaseFeature = -> Pad009
  MirrorPlane = -> YZ_Plane009
  Originals = -> [Pad009]
  Placement = pos=(0,0,0) rot=(1,0,0;1.5708rad)
FEATURE [Sketcher::SketchObject] Sketch020  label="Side mounting holes spec"
  ExternalGeometry = -> [Mirrored004]
  FullyConstrained = false
  MapMode = 5
  Placement = pos=(59.85,-1.32e-14,1.32e-14) rot=(0.707107,0,0.707107;3.14159rad)
  Support = -> [Mirrored004]
  sketch-geometry (6):
    g0: Circle CenterX=16 CenterY=-7 CenterZ=0 NormalX=0 NormalY=0 NormalZ=1 AngleXU=0 Radius=2.25
    g1: Circle CenterX=52 CenterY=-7 CenterZ=0 NormalX=0 NormalY=0 NormalZ=1 AngleXU=0 Radius=2.25
    g2: LineSegment StartX=52 StartY=-7 StartZ=0 EndX=52 EndY=-13.5 EndZ=0
    g3: LineSegment StartX=52 StartY=-7 StartZ=0 EndX=58 EndY=-7 EndZ=0
    g4: LineSegment StartX=52 StartY=-7 StartZ=0 EndX=16 EndY=-7 EndZ=0
    g5: LineSegment StartX=16 StartY=-7 StartZ=0 EndX=16 EndY=-13.5 EndZ=0
  constraints (15):
    c: Coincident(g2,g1)
    c: Coincident(g2,g3)
    c: Horizontal(g3)
    c: PointOnObject(g2,g-5)
    c: Symmetric(g-6,g-5,g2)
    c: PointOnObject(g3,g-6)
    c: DistanceY(g3,g-6) = 7
    c: Coincident(g4,g1)
    c: Coincident(g4,g0)
    c: Horizontal(g4)
    c: Coincident(g5,g0)
    c: Perpendicular(g5,g-3) = 4.71239
    c: Symmetric(g-3,g-4,g5)
    c: Radius(g0) = 2.25
    c: Equal(g0,g1)
FEATURE [PartDesign::Pocket] Pocket009  label="Add side mounting holes"
  AllowMultiFace = false
  BaseFeature = -> Mirrored004
  Length = 5
  Length2 = 100
  Placement = pos=(0,0,0) rot=(1,0,0;1.5708rad)
  Profile = -> Sketch020
  Type = 1
FEATURE [Sketcher::SketchObject] Sketch021  label="Side mounting holes nut trap spec"
  ExternalGeometry = -> [Pocket009]
  FullyConstrained = false
  MapMode = 5
  Placement = pos=(-53.85,0,0) rot=(0.707107,0,0.707107;3.14159rad)
  Support = -> [Pocket009]
  sketch-geometry (14):
    g0: LineSegment StartX=19.5 StartY=-9.02073 StartZ=0 EndX=19.5 EndY=-4.97927 EndZ=0
    g1: LineSegment StartX=19.5 StartY=-4.97927 StartZ=0 EndX=16 EndY=-2.95855 EndZ=0
    g2: LineSegment StartX=16 StartY=-2.95855 StartZ=0 EndX=12.5 EndY=-4.97927 EndZ=0
    g3: LineSegment StartX=12.5 StartY=-4.97927 StartZ=0 EndX=12.5 EndY=-9.02073 EndZ=0
    g4: LineSegment StartX=12.5 StartY=-9.02073 StartZ=0 EndX=16 EndY=-11.0415 EndZ=0
    g5: LineSegment StartX=16 StartY=-11.0415 StartZ=0 EndX=19.5 EndY=-9.02073 EndZ=0
    g6: Circle CenterX=16 CenterY=-7 CenterZ=0 NormalX=0 NormalY=0 NormalZ=1 AngleXU=0 Radius=4.04145
    g7: LineSegment StartX=55.5 StartY=-9.02073 StartZ=0 EndX=55.5 EndY=-4.97927 EndZ=0
    g8: LineSegment StartX=55.5 StartY=-4.97927 StartZ=0 EndX=52 EndY=-2.95855 EndZ=0
    g9: LineSegment StartX=52 StartY=-2.95855 StartZ=0 EndX=48.5 EndY=-4.97927 EndZ=0
    g10: LineSegment StartX=48.5 StartY=-4.97927 StartZ=0 EndX=48.5 EndY=-9.02073 EndZ=0
    g11: LineSegment StartX=48.5 StartY=-9.02073 StartZ=0 EndX=52 EndY=-11.0415 EndZ=0
    g12: LineSegment StartX=52 StartY=-11.0415 StartZ=0 EndX=55.5 EndY=-9.02073 EndZ=0
    g13: Circle CenterX=52 CenterY=-7 CenterZ=0 NormalX=0 NormalY=0 NormalZ=1 AngleXU=0 Radius=4.04145
  constraints (32):
    c: Coincident(g0,g1)
    c: Coincident(g1,g2)
    c: Coincident(g2,g3)
    c: Coincident(g3,g4)
    c: Coincident(g4,g5)
    c: Coincident(g5,g0)
    c: Equal(g0, g1-g5) x5
    c: PointOnObject(g0,g6)
    c: PointOnObject(g1,g6)
    c: PointOnObject(g2,g6)
    c: PointOnObject(g3,g6)
    c: PointOnObject(g4,g6)
    c: PointOnObject(g5,g6)
    c: Coincident(g7,g8)
    c: Coincident(g8,g9)
    c: Coincident(g9,g10)
    c: Coincident(g10,g11)
    c: Coincident(g11,g12)
    c: Coincident(g12,g7)
    c: Equal(g7, g8-g12) x5
    c: PointOnObject(g7,g13)
    c: PointOnObject(g8,g13)
    c: PointOnObject(g9,g13)
    c: PointOnObject(g10,g13)
    c: PointOnObject(g11,g13)
    c: PointOnObject(g12,g13)
    c: Vertical(g0)
    c: Vertical(g7)
    c: Coincident(g6,g-3)
    c: Coincident(g13,g-4)
    c: Distance(g2,g0) = 7
    c: Equal(g13,g6)
FEATURE [PartDesign::Pocket] Pocket010  label="Add side mounting nut-traps"
  AllowMultiFace = false
  BaseFeature = -> Pocket009
  Length = 3.5
  Length2 = 100
  Placement = pos=(0,0,0) rot=(1,0,0;1.5708rad)
  Profile = -> Sketch021
  Type = 0
FEATURE [Sketcher::SketchObject] Sketch022  label="Barrel-jack cutout spec"
  FullyConstrained = false
  MapMode = 5
  Placement = pos=(0,-3,-7e-16) rot=(1,0,0;1.5708rad)
  Support = -> [Pocket010]
  sketch-geometry (5):
    g0: LineSegment StartX=10.75 StartY=24.5 StartZ=0 EndX=21.25 EndY=24.5 EndZ=0
    g1: LineSegment StartX=21.25 StartY=24.5 StartZ=0 EndX=21.25 EndY=12 EndZ=0
    g2: LineSegment StartX=21.25 StartY=12 StartZ=0 EndX=10.75 EndY=12 EndZ=0
    g3: LineSegment StartX=10.75 StartY=12 StartZ=0 EndX=10.75 EndY=24.5 EndZ=0
    g4: LineSegment StartX=16 StartY=24.5 StartZ=0 EndX=16 EndY=12 EndZ=0
  constraints (14):
    c: Coincident(g0,g1)
    c: Coincident(g1,g2)
    c: Coincident(g2,g3)
    c: Coincident(g3,g0)
    c: Horizontal(g0)
    c: Vertical(g1)
    c: Vertical(g3)
    c: Distance(g0) = 10.5
    c: Distance(g3) = 12.5
    c: DistanceY(g1) = 12
    c: Perpendicular(g4,g2) = 4.71239
    c: Perpendicular(g4,g0) = 1.5708
    c: Symmetric(g0,g0,g4)
    c: DistanceX(g4) = 16
FEATURE [PartDesign::Pocket] Pocket011  label="Add barrel-jack cutout"
  AllowMultiFace = false
  BaseFeature = -> Pocket010
  Length = 5
  Length2 = 100
  Placement = pos=(0,0,0) rot=(1,0,0;1.5708rad)
  Profile = -> Sketch022
  Type = 1
FEATURE [PartDesign::Chamfer] Chamfer002
  Angle = 45
  Base = -> Pocket011 [Face5]
  BaseFeature = -> Pocket011
  ChamferType = 0
  FlipDirection = false
  Placement = pos=(0,0,0) rot=(1,0,0;1.5708rad)
  Size = 1
  Size2 = 1
  SupportTransform = false
FEATURE [Sketcher::SketchObject] Sketch023
  FullyConstrained = false
  MapMode = 5
  Placement = pos=(0,0,0) rot=(1,0,0;1.5708rad)
  Support = -> [XZ_Plane010]
  sketch-geometry (7):
    g0: LineSegment StartX=2.25 StartY=0 StartZ=0 EndX=2.25 EndY=2.5 EndZ=0
    g1: LineSegment StartX=2.25 StartY=2.5 StartZ=0 EndX=8.55796 EndY=2.5 EndZ=0
    g2: LineSegment StartX=8.55796 StartY=2.5 StartZ=0 EndX=8.55796 EndY=0 EndZ=0
    g3: LineSegment StartX=8.55796 StartY=0 StartZ=0 EndX=7.5 EndY=-6 EndZ=0
    g4: LineSegment StartX=7.5 StartY=-6 StartZ=0 EndX=4.25 EndY=-6 EndZ=0
    g5: LineSegment StartX=4.25 StartY=-6 StartZ=0 EndX=4.25 EndY=0 EndZ=0
    g6: LineSegment StartX=4.25 StartY=0 StartZ=0 EndX=2.25 EndY=0 EndZ=0
  constraints (21):
    c: Coincident(g0,g1)
    c: Coincident(g1,g2)
    c: Coincident(g2,g3)
    c: Coincident(g3,g4)
    c: Coincident(g4,g5)
    c: Coincident(g5,g6)
    c: Horizontal(g4)
    c: Horizontal(g1)
    c: Horizontal(g6)
    c: Coincident(g0,g6)
    c: Vertical(g0)
    c: DistanceX(g0) = 2.25
    c: PointOnObject(g0,g-1)
    c: Vertical(g5)
    c: Vertical(g2)
    c: Distance(g0) = 2.5
    c: Distance(g2) = 2.5
    c: DistanceX(g5) = 4.25
    c: Distance(g5) = 6
    c: Distance(g4) = 3.25
    c: Angle(g3,g4) = 1.74533
FEATURE [PartDesign::Revolution] Revolution001
  AllowMultiFace = false
  Angle = 360
  Axis = (0,2e-16,1)
  Base = (0,0,0)
  Placement = pos=(0,0,0) rot=(1,0,0;1.5708rad)
  Profile = -> Sketch023
  ReferenceAxis = -> Sketch023 [V_Axis]
  Reversed = true
FEATURE [PartDesign::Fillet] Fillet002
  Base = -> Revolution001 [Face5]
  BaseFeature = -> Revolution001
  Placement = pos=(0,0,0) rot=(1,0,0;1.5708rad)
  Radius = 0.5
  SupportTransform = false
FEATURE [PartDesign::Chamfer] Chamfer003
  Angle = 45
  Base = -> Fillet002 [Face5]
  BaseFeature = -> Fillet002
  ChamferType = 0
  FlipDirection = false
  Placement = pos=(0,0,0) rot=(1,0,0;1.5708rad)
  Size = 0.4
  Size2 = 1
  SupportTransform = false
FEATURE [PartDesign::Body] Body006  label="Foot001"
  Group = -> [Sketch023,Revolution001,Fillet002,Chamfer003]
  Origin = -> Origin010
  Placement = pos=(-49,-53,0) rot=(0,0,1;0rad)
  Tip = -> Chamfer003
FEATURE [Part::FeaturePython] Array004  label="Foot array"  # Draft array (typed FeaturePython)
  Angle = 360
  ArrayType = 0
  Axis = (0,0,1)
  Base = -> Body006
  Center = (0,0,0)
  Fuse = false
  IntervalAxis = (0,0,0)
  IntervalX = (98,0,0)
  IntervalY = (0,106,0)
  IntervalZ = (0,0,1)
  NumberPolar = 1
  NumberX = 2
  NumberY = 2
  NumberZ = 1
  Placement = pos=(0,0,-3) rot=(0,0,1;0rad)
FEATURE [PartDesign::Chamfer] Chamfer004
  Angle = 45
  Base = -> Pocket005 [Face5]
  BaseFeature = -> Pocket005
  ChamferType = 0
  FlipDirection = false
  Placement = pos=(0,0,0) rot=(1,0,0;1.5708rad)
  Size = 1
  Size2 = 1
  SupportTransform = false
FEATURE [PartDesign::Chamfer] Chamfer005
  Angle = 45
  Base = -> Chamfer004 [Edge1,Edge4]
  BaseFeature = -> Chamfer004
  ChamferType = 0
  FlipDirection = false
  Placement = pos=(0,0,0) rot=(1,0,0;1.5708rad)
  Size = 1
  Size2 = 1
  SupportTransform = false
FEATURE [PartDesign::Chamfer] Chamfer006
  Angle = 45
  Base = -> Chamfer001 [Edge8]
  BaseFeature = -> Chamfer001
  ChamferType = 0
  FlipDirection = false
  Placement = pos=(0,0,0) rot=(1,0,0;1.5708rad)
  Size = 1
  Size2 = 1
  SupportTransform = false
FEATURE [PartDesign::Chamfer] Chamfer007
  Angle = 45
  Base = -> Chamfer002 [Edge1,Edge4]
  BaseFeature = -> Chamfer002
  ChamferType = 0
  FlipDirection = false
  Placement = pos=(0,0,0) rot=(1,0,0;1.5708rad)
  Size = 1
  Size2 = 1
  SupportTransform = false
FEATURE [PartDesign::Chamfer] Chamfer008
  Angle = 45
  Base = -> Chamfer005 [Edge43,Edge42]
  BaseFeature = -> Chamfer005
  ChamferType = 0
  FlipDirection = false
  Placement = pos=(0,0,0) rot=(1,0,0;1.5708rad)
  Size = 1
  Size2 = 1
  SupportTransform = false
FEATURE [PartDesign::Chamfer] Chamfer009
  Angle = 45
  Base = -> Chamfer007 [Edge50,Edge51]
  BaseFeature = -> Chamfer007
  ChamferType = 0
  FlipDirection = false
  Placement = pos=(0,0,0) rot=(1,0,0;1.5708rad)
  Size = 1
  Size2 = 1
  SupportTransform = false
FEATURE [PartDesign::Mirrored] Mirrored005  label="Add other side mounting nut traps"
  BaseFeature = -> Chamfer008
  MirrorPlane = -> YZ_Plane008
  Originals = -> [Pocket005]
  Placement = pos=(0,0,0) rot=(1,0,0;1.5708rad)
FEATURE [Sketcher::SketchObject] Sketch024  label="Switchgear holes spec"
  ExternalGeometry = -> [Mirrored005]
  FullyConstrained = false
  MapMode = 5
  Placement = pos=(0,-3,-7e-16) rot=(1,0,0;1.5708rad)
  Support = -> [Mirrored005]
  sketch-geometry (13):
    g0: LineSegment StartX=-40.725 StartY=43.625 StartZ=0 EndX=-33.675 EndY=43.625 EndZ=0
    g1: LineSegment StartX=-33.675 StartY=43.625 StartZ=0 EndX=-33.675 EndY=24.375 EndZ=0
    g2: LineSegment StartX=-33.675 StartY=24.375 StartZ=0 EndX=-40.725 EndY=24.375 EndZ=0
    g3: LineSegment StartX=-40.725 StartY=24.375 StartZ=0 EndX=-40.725 EndY=43.625 EndZ=0
    g4: LineSegment StartX=-40.725 StartY=43.625 StartZ=0 EndX=-33.675 EndY=24.375 EndZ=0
    g5: LineSegment StartX=-33.675 StartY=43.625 StartZ=0 EndX=-40.725 EndY=24.375 EndZ=0
    g6: GeomPoint X=-37.2 Y=34 Z=0
    g7: Circle CenterX=-12.4 CenterY=34 CenterZ=0 NormalX=0 NormalY=0 NormalZ=1 AngleXU=0 Radius=2.65
    g8: Circle CenterX=37.2 CenterY=34 CenterZ=0 NormalX=0 NormalY=0 NormalZ=1 AngleXU=0 Radius=8.15
    g9: LineSegment StartX=-37.2 StartY=34 StartZ=0 EndX=-12.4 EndY=34 EndZ=0
    g10: LineSegment StartX=-12.4 StartY=34 StartZ=0 EndX=12.4 EndY=34 EndZ=0
    g11: LineSegment StartX=12.4 StartY=34 StartZ=0 EndX=37.2 EndY=34 EndZ=0
    g12: LineSegment StartX=-37.2 StartY=34 StartZ=0 EndX=-62 EndY=34 EndZ=0
  constraints (32):
    c: Coincident(g0,g1)
    c: Coincident(g1,g2)
    c: Coincident(g2,g3)
    c: Coincident(g3,g0)
    c: Horizontal(g0)
    c: Horizontal(g2)
    c: Vertical(g1)
    c: Vertical(g3)
    c: Distance(g1) = 19.25
    c: Distance(g0) = 7.05
    c: Coincident(g4,g0)
    c: Coincident(g5,g0)
    c: Coincident(g4,g1)
    c: Coincident(g5,g2)
    c: PointOnObject(g6,g4)
    c: PointOnObject(g6,g5)
    c: Radius(g7) = 2.65
    c: Coincident(g7,g9)
    c: Coincident(g9,g6)
    c: Horizontal(g9)
    c: Equal(g11,g10)
    c: Equal(g10,g9)
    c: Horizontal(g10)
    c: Coincident(g10,g11)
    c: Coincident(g10,g7)
    c: Coincident(g11,g8)
    c: Coincident(g6,g12)
    c: Perpendicular(g12,g-3) = 4.71239
    c: Symmetric(g6,g8,g-2)
    c: Equal(g12,g9)
    c: Symmetric(g-3,g-3,g12)
    c: Radius(g8) = 8.15
FEATURE [PartDesign::Pocket] Pocket012  label="Add switchgear holes"
  AllowMultiFace = false
  BaseFeature = -> Mirrored005
  Length = 5
  Length2 = 100
  Placement = pos=(0,0,0) rot=(1,0,0;1.5708rad)
  Profile = -> Sketch024
  Type = 1
FEATURE [Sketcher::SketchObject] Sketch025  label="Switch backface thinning tool"
  ExternalGeometry = -> [Pocket012]
  FullyConstrained = false
  MapMode = 5
  Placement = pos=(0,-1e-16,0) rot=(-1,0,0;1.5708rad)
  Support = -> [Pocket012]
  sketch-geometry (6):
    g0: LineSegment StartX=-40.725 StartY=-20.375 StartZ=0 EndX=-33.675 EndY=-20.375 EndZ=0
    g1: LineSegment StartX=-33.675 StartY=-20.375 StartZ=0 EndX=-33.675 EndY=-43.625 EndZ=0
    g2: LineSegment StartX=-33.675 StartY=-47.625 StartZ=0 EndX=-40.725 EndY=-47.625 EndZ=0
    g3: LineSegment StartX=-40.725 StartY=-47.625 StartZ=0 EndX=-40.725 EndY=-24.375 EndZ=0
    g4: LineSegment StartX=-33.675 StartY=-43.625 StartZ=0 EndX=-33.675 EndY=-47.625 EndZ=0
    g5: LineSegment StartX=-40.725 StartY=-24.375 StartZ=0 EndX=-40.725 EndY=-20.375 EndZ=0
  constraints (16):
    c: Coincident(g0,g1)
    c: Coincident(g2,g3)
    c: Horizontal(g0)
    c: Horizontal(g2)
    c: Vertical(g1)
    c: Vertical(g3)
    c: Coincident(g1,g4)
    c: Coincident(g1,g-4)
    c: Coincident(g4,g2)
    c: Vertical(g4)
    c: Coincident(g3,g-3)
    c: Coincident(g3,g5)
    c: Coincident(g5,g0)
    c: Vertical(g5)
    c: Equal(g5,g4)
    c: Distance(g5) = 4
FEATURE [PartDesign::Pocket] Pocket013  label="Thin backwall for switch to 2mm"
  AllowMultiFace = false
  BaseFeature = -> Pocket012
  Length = 1
  Length2 = 100
  Placement = pos=(0,0,0) rot=(1,0,0;1.5708rad)
  Profile = -> Sketch025
  Type = 0
FEATURE [PartDesign::Mirrored] Mirrored006  label="Add other side nut traps"
  BaseFeature = -> Chamfer009
  MirrorPlane = -> YZ_Plane009
  Originals = -> [Pocket010]
  Placement = pos=(0,0,0) rot=(1,0,0;1.5708rad)
FEATURE [PartDesign::Chamfer] Chamfer010  label="Make LED hole pretty chamfer"
  Angle = 45
  Base = -> Pocket013 [Edge101]
  BaseFeature = -> Pocket013
  ChamferType = 0
  FlipDirection = false
  Placement = pos=(0,0,0) rot=(1,0,0;1.5708rad)
  Size = 2
  Size2 = 1
  SupportTransform = false
FEATURE [Sketcher::SketchObject] Sketch026  label="Decorative feature for LED hole"
  ExternalGeometry = -> [Chamfer010]
  FullyConstrained = false
  MapMode = 5
  Placement = pos=(0,-3,-7e-16) rot=(1,0,0;1.5708rad)
  Support = -> [Chamfer010]
  sketch-geometry (4):
    g0: Circle CenterX=-12.4 CenterY=34 CenterZ=0 NormalX=0 NormalY=0 NormalZ=1 AngleXU=0 Radius=6.65
    g1: Circle CenterX=-12.4 CenterY=34 CenterZ=0 NormalX=0 NormalY=0 NormalZ=1 AngleXU=0 Radius=8.4
    g2: LineSegment StartX=-12.4 StartY=38.65 StartZ=0 EndX=-12.4 EndY=40.65 EndZ=0
    g3: LineSegment StartX=-5.75 StartY=34 StartZ=0 EndX=-4 EndY=34 EndZ=0
  constraints (10):
    c: Coincident(g0,g1)
    c: Coincident(g0,g-3)
    c: Perpendicular(g2,g-3) = 1.5708
    c: PointOnObject(g2,g0)
    c: Distance(g2) = 2
    c: Vertical(g2)
    c: Horizontal(g3)
    c: Perpendicular(g3,g0) = 1.5708
    c: PointOnObject(g3,g1)
    c: Distance(g3) = 1.75
FEATURE [PartDesign::Pocket] Pocket014  label="Add decorative feature for LED hole"
  AllowMultiFace = false
  BaseFeature = -> Chamfer010
  Length = 1.5
  Length2 = 100
  Placement = pos=(0,0,0) rot=(1,0,0;1.5708rad)
  Profile = -> Sketch026
  Type = 0
FEATURE [PartDesign::Chamfer] Chamfer011  label="Decorative feature easing chamfer"
  Angle = 45
  Base = -> Pocket014 [Edge39,Edge200]
  BaseFeature = -> Pocket014
  ChamferType = 0
  FlipDirection = false
  Placement = pos=(0,0,0) rot=(1,0,0;1.5708rad)
  Size = 0.35
  Size2 = 1
  SupportTransform = false
FEATURE [PartDesign::Chamfer] Chamfer012  label="Switchgear easing-in chamfers"
  Angle = 45
  Base = -> Chamfer011 [Edge206,Edge184,Edge188,Edge205,Edge128]
  BaseFeature = -> Chamfer011
  ChamferType = 0
  FlipDirection = false
  Placement = pos=(0,0,0) rot=(1,0,0;1.5708rad)
  Size = 0.3
  Size2 = 1
  SupportTransform = false
FEATURE [Sketcher::SketchObject] Sketch027  label="Joining Bar spec"
  FullyConstrained = false
  MapMode = 5
  Placement = pos=(0,0,0) rot=(0.57735,0.57735,0.57735;2.0944rad)
  Support = -> [YZ_Plane011]
  sketch-geometry (20):
    g0: LineSegment StartX=-37.25 StartY=83.9 StartZ=0 EndX=-37.25 EndY=72.1 EndZ=0
    g1: LineSegment StartX=-37.25 StartY=72.1 StartZ=0 EndX=37.25 EndY=72.1 EndZ=0
    g2: LineSegment StartX=37.25 StartY=72.1 StartZ=0 EndX=37.25 EndY=83.9 EndZ=0
    g3: LineSegment StartX=37.25 StartY=83.9 StartZ=0 EndX=52.75 EndY=83.9 EndZ=0
    g4: LineSegment StartX=52.75 StartY=83.9 StartZ=0 EndX=52.75 EndY=52.3 EndZ=0
    g5: LineSegment StartX=52.75 StartY=52.3 StartZ=0 EndX=37.25 EndY=52.3 EndZ=0
    g6: LineSegment StartX=37.25 StartY=52.3 StartZ=0 EndX=37.25 EndY=64.1 EndZ=0
    g7: LineSegment StartX=37.25 StartY=64.1 StartZ=0 EndX=-37.25 EndY=64.1 EndZ=0
    g8: LineSegment StartX=-37.25 StartY=64.1 StartZ=0 EndX=-37.25 EndY=52.3 EndZ=0
    g9: LineSegment StartX=-37.25 StartY=52.3 StartZ=0 EndX=-52.75 EndY=52.3 EndZ=0
    g10: LineSegment StartX=-52.75 StartY=52.3 StartZ=0 EndX=-52.75 EndY=83.9 EndZ=0
    g11: LineSegment StartX=-52.75 StartY=83.9 StartZ=0 EndX=-37.25 EndY=83.9 EndZ=0
    g12: Circle CenterX=45 CenterY=60.05 CenterZ=0 NormalX=0 NormalY=0 NormalZ=1 AngleXU=0 Radius=2.25
    g13: Circle CenterX=45 CenterY=76.15 CenterZ=0 NormalX=0 NormalY=0 NormalZ=1 AngleXU=0 Radius=2.25
    g14: LineSegment StartX=45 StartY=57.8 StartZ=0 EndX=45 EndY=52.3 EndZ=0
    g15: LineSegment StartX=42.75 StartY=60.05 StartZ=0 EndX=37.25 EndY=60.05 EndZ=0
    g16: LineSegment StartX=47.25 StartY=60.05 StartZ=0 EndX=52.75 EndY=60.05 EndZ=0
    g17: Circle CenterX=-45 CenterY=76.15 CenterZ=0 NormalX=0 NormalY=0 NormalZ=1 AngleXU=0 Radius=2.25
    g18: Circle CenterX=-45 CenterY=60.05 CenterZ=0 NormalX=0 NormalY=0 NormalZ=1 AngleXU=0 Radius=2.25
    g19: LineSegment StartX=52.75 StartY=68.1 StartZ=0 EndX=-52.75 EndY=68.1 EndZ=0
  constraints (52):
    c: Coincident(g0,g1)
    c: Coincident(g1,g2)
    c: Coincident(g2,g3)
    c: Coincident(g3,g4)
    c: Coincident(g4,g5)
    c: Coincident(g5,g6)
    c: Coincident(g6,g7)
    c: Coincident(g7,g8)
    c: Coincident(g8,g9)
    c: Coincident(g9,g10)
    c: Coincident(g10,g11)
    c: Coincident(g11,g0)
    c: Horizontal(g11)
    c: Horizontal(g9)
    c: Horizontal(g7)
    c: Horizontal(g3)
    c: Horizontal(g5)
    c: Vertical(g10)
    c: Vertical(g0)
    c: Vertical(g8)
    c: Vertical(g2)
    c: Vertical(g6)
    c: Equal(g3,g5)
    c: Equal(g5,g9)
    c: Equal(g9,g11)
    c: Equal(g0,g8)
    c: Equal(g8,g2)
    c: Equal(g2,g6)
    c: Symmetric(g1,g0,g-2)
    c: Distance(g0,g7) = 8
    c: Distance(g13,g12) = 16.1
    c: Perpendicular(g16,g12) = 1.5708
    c: Perpendicular(g15,g12) = 1.5708
    c: Perpendicular(g16,g4) = 4.71239
    c: Perpendicular(g15,g6) = 4.71239
    c: Perpendicular(g14,g12) = 1.5708
    c: Perpendicular(g14,g5) = 4.71239
    c: Radius(g17) = 2.25
    c: Equal(g17,g18)
    c: Equal(g17,g13)
    c: Equal(g17,g12)
    c: Perpendicular(g19,g10) = 4.71239
    c: Perpendicular(g19,g4) = 1.5708
    c: Symmetric(g9,g10,g19)
    c: Symmetric(g17,g18,g19)
    c: Symmetric(g13,g12,g19)
    c: Equal(g15,g16)
    c: Equal(g15,g14)
    c: Symmetric(g18,g12,g-2)
    c: Distance(g15) = 5.5
    c: Distance(g17,g13) = 90
    c: DistanceY(g19) = 68.1
FEATURE [PartDesign::Pad] Pad010  label="Make Joining bar"
  AllowMultiFace = false
  Direction = (1,1,1)
  Length = 3.5
  Length2 = 100
  Placement = pos=(0,0,0) rot=(0.57735,0.57735,0.57735;2.0944rad)
  Profile = -> Sketch027
  Type = 0
FEATURE [Sketcher::SketchObject] Sketch028  label="Nut trap outer walls"
  ExternalGeometry = -> [Pad010]
  FullyConstrained = false
  MapMode = 5
  Placement = pos=(-1e-16,0,0) rot=(0.57735,0.57735,-0.57735;4.18879rad)
  Support = -> [Pad010]
  sketch-geometry (16):
    g0: LineSegment StartX=48.7528 StartY=-66.55 StartZ=0 EndX=52.5056 EndY=-60.05 EndZ=0
    g1: LineSegment StartX=52.5056 StartY=-60.05 StartZ=0 EndX=48.7528 EndY=-53.55 EndZ=0
    g2: LineSegment StartX=48.7528 StartY=-53.55 StartZ=0 EndX=41.2472 EndY=-53.55 EndZ=0
    g3: LineSegment StartX=41.2472 StartY=-53.55 StartZ=0 EndX=37.4944 EndY=-60.05 EndZ=0
    g4: LineSegment StartX=37.4944 StartY=-60.05 StartZ=0 EndX=41.2472 EndY=-66.55 EndZ=0
    g5: LineSegment StartX=41.2472 StartY=-66.55 StartZ=0 EndX=48.7528 EndY=-66.55 EndZ=0
    g6: Circle CenterX=45 CenterY=-60.05 CenterZ=0 NormalX=0 NormalY=0 NormalZ=1 AngleXU=0 Radius=7.50555
    g7: LineSegment StartX=48.7528 StartY=-82.65 StartZ=0 EndX=52.5056 EndY=-76.15 EndZ=0
    g8: LineSegment StartX=52.5056 StartY=-76.15 StartZ=0 EndX=48.7528 EndY=-69.65 EndZ=0
    g9: LineSegment StartX=48.7528 StartY=-69.65 StartZ=0 EndX=41.2472 EndY=-69.65 EndZ=0
    g10: LineSegment StartX=41.2472 StartY=-69.65 StartZ=0 EndX=37.4944 EndY=-76.15 EndZ=0
    g11: LineSegment StartX=37.4944 StartY=-76.15 StartZ=0 EndX=41.2472 EndY=-82.65 EndZ=0
    g12: LineSegment StartX=41.2472 StartY=-82.65 StartZ=0 EndX=48.7528 EndY=-82.65 EndZ=0
    g13: Circle CenterX=45 CenterY=-76.15 CenterZ=0 NormalX=0 NormalY=0 NormalZ=1 AngleXU=0 Radius=7.50555
    g14: Circle CenterX=45 CenterY=-60.05 CenterZ=0 NormalX=0 NormalY=0 NormalZ=1 AngleXU=0 Radius=2.25
    g15: Circle CenterX=45 CenterY=-76.15 CenterZ=0 NormalX=0 NormalY=0 NormalZ=1 AngleXU=0 Radius=2.25
  constraints (36):
    c: Coincident(g0,g1)
    c: Coincident(g1,g2)
    c: Coincident(g2,g3)
    c: Coincident(g3,g4)
    c: Coincident(g4,g5)
    c: Coincident(g5,g0)
    c: Equal(g0, g1-g5) x5
    c: PointOnObject(g0,g6)
    c: PointOnObject(g1,g6)
    c: PointOnObject(g2,g6)
    c: PointOnObject(g3,g6)
    c: PointOnObject(g4,g6)
    c: PointOnObject(g5,g6)
    c: Horizontal(g2)
    c: Coincident(g7,g8)
    c: Coincident(g8,g9)
    c: Coincident(g9,g10)
    c: Coincident(g10,g11)
    c: Coincident(g11,g12)
    c: Coincident(g12,g7)
    c: Equal(g7, g8-g12) x5
    c: PointOnObject(g7,g13)
    c: PointOnObject(g8,g13)
    c: PointOnObject(g9,g13)
    c: PointOnObject(g10,g13)
    c: PointOnObject(g11,g13)
    c: PointOnObject(g12,g13)
    c: Horizontal(g9)
    c: Equal(g13,g6)
    c: Distance(g2,g4) = 13
    c: Coincident(g6,g-4)
    c: Coincident(g13,g-3)
    c: Coincident(g15,g13)
    c: Coincident(g14,g6)
    c: Equal(g14,g15)
    c: Equal(g15,g-3)
FEATURE [PartDesign::Pad] Pad011  label="Add nut trap outer walls"
  AllowMultiFace = false
  BaseFeature = -> Pad010
  Direction = (1,1,1)
  Length = 2.5
  Length2 = 100
  Placement = pos=(0,0,0) rot=(0.57735,0.57735,0.57735;2.0944rad)
  Profile = -> Sketch028
  Type = 0
FEATURE [PartDesign::Mirrored] Mirrored007  label="Add mirror of nut trap outer walls"
  BaseFeature = -> Pad011
  MirrorPlane = -> Sketch028 [V_Axis]
  Originals = -> [Pad011]
  Placement = pos=(0,0,0) rot=(0.57735,0.57735,0.57735;2.0944rad)
FEATURE [Sketcher::SketchObject] Sketch029  label="Nut trap spec for bar"
  ExternalGeometry = -> [Mirrored007]
  FullyConstrained = false
  MapMode = 5
  Placement = pos=(-2.5,1.1e-15,-1.1e-15) rot=(0.57735,0.57735,-0.57735;4.18879rad)
  Support = -> [Mirrored007]
  sketch-geometry (14):
    g0: LineSegment StartX=-42.9793 StartY=-63.55 StartZ=0 EndX=-40.9585 EndY=-60.05 EndZ=0
    g1: LineSegment StartX=-40.9585 StartY=-60.05 StartZ=0 EndX=-42.9793 EndY=-56.55 EndZ=0
    g2: LineSegment StartX=-42.9793 StartY=-56.55 StartZ=0 EndX=-47.0207 EndY=-56.55 EndZ=0
    g3: LineSegment StartX=-47.0207 StartY=-56.55 StartZ=0 EndX=-49.0415 EndY=-60.05 EndZ=0
    g4: LineSegment StartX=-49.0415 StartY=-60.05 StartZ=0 EndX=-47.0207 EndY=-63.55 EndZ=0
    g5: LineSegment StartX=-47.0207 StartY=-63.55 StartZ=0 EndX=-42.9793 EndY=-63.55 EndZ=0
    g6: Circle CenterX=-45 CenterY=-60.05 CenterZ=0 NormalX=0 NormalY=0 NormalZ=1 AngleXU=0 Radius=4.04145
    g7: LineSegment StartX=-42.9793 StartY=-79.65 StartZ=0 EndX=-40.9585 EndY=-76.15 EndZ=0
    g8: LineSegment StartX=-40.9585 StartY=-76.15 StartZ=0 EndX=-42.9793 EndY=-72.65 EndZ=0
    g9: LineSegment StartX=-42.9793 StartY=-72.65 StartZ=0 EndX=-47.0207 EndY=-72.65 EndZ=0
    g10: LineSegment StartX=-47.0207 StartY=-72.65 StartZ=0 EndX=-49.0415 EndY=-76.15 EndZ=0
    g11: LineSegment StartX=-49.0415 StartY=-76.15 StartZ=0 EndX=-47.0207 EndY=-79.65 EndZ=0
    g12: LineSegment StartX=-47.0207 StartY=-79.65 StartZ=0 EndX=-42.9793 EndY=-79.65 EndZ=0
    g13: Circle CenterX=-45 CenterY=-76.15 CenterZ=0 NormalX=0 NormalY=0 NormalZ=1 AngleXU=0 Radius=4.04145
  constraints (32):
    c: Coincident(g0,g1)
    c: Coincident(g1,g2)
    c: Coincident(g2,g3)
    c: Coincident(g3,g4)
    c: Coincident(g4,g5)
    c: Coincident(g5,g0)
    c: Equal(g0, g1-g5) x5
    c: PointOnObject(g0,g6)
    c: PointOnObject(g1,g6)
    c: PointOnObject(g2,g6)
    c: PointOnObject(g3,g6)
    c: PointOnObject(g4,g6)
    c: PointOnObject(g5,g6)
    c: Coincident(g7,g8)
    c: Coincident(g8,g9)
    c: Coincident(g9,g10)
    c: Coincident(g10,g11)
    c: Coincident(g11,g12)
    c: Coincident(g12,g7)
    c: Equal(g7, g8-g12) x5
    c: PointOnObject(g7,g13)
    c: PointOnObject(g8,g13)
    c: PointOnObject(g9,g13)
    c: PointOnObject(g10,g13)
    c: PointOnObject(g11,g13)
    c: PointOnObject(g12,g13)
    c: Horizontal(g5)
    c: Horizontal(g9)
    c: Coincident(g6,g-3)
    c: Coincident(g13,g-4)
    c: Equal(g6,g13)
    c: Distance(g0,g1) = 7
FEATURE [PartDesign::Pocket] Pocket015  label="Add nut traps for bar"
  AllowMultiFace = false
  BaseFeature = -> Mirrored007
  Length = 4
  Length2 = 100
  Placement = pos=(0,0,0) rot=(0.57735,0.57735,0.57735;2.0944rad)
  Profile = -> Sketch029
  Type = 0
FEATURE [PartDesign::Mirrored] Mirrored008  label="Add other nut traps for bar"
  BaseFeature = -> Pocket015
  MirrorPlane = -> XZ_Plane011
  Originals = -> [Pocket015]
  Placement = pos=(0,0,0) rot=(0.57735,0.57735,0.57735;2.0944rad)
FEATURE [PartDesign::Fillet] Fillet003  label="Round corners off and Dogbone!"
  Base = -> Mirrored008 [Edge8,Edge58,Edge1,Edge2,Edge5,Edge60,Edge63,Edge64,Edge62,Edge59,Edge57,Edge61]
  BaseFeature = -> Mirrored008
  Placement = pos=(0,0,0) rot=(0.57735,0.57735,0.57735;2.0944rad)
  Radius = 4
  SupportTransform = false
FEATURE [PartDesign::Chamfer] Chamfer013  label="Screw penetration aid chamfers"
  Angle = 45
  Base = -> Fillet003 [Face52,Face51,Face54,Face53]
  BaseFeature = -> Fillet003
  ChamferType = 0
  FlipDirection = false
  Placement = pos=(0,0,0) rot=(0.57735,0.57735,0.57735;2.0944rad)
  Size = 0.35
  Size2 = 1
  SupportTransform = false
FEATURE [PartDesign::Chamfer] Chamfer014  label="Print and fitting aid chamfer"
  Angle = 45
  Base = -> Chamfer013 [Edge6]
  BaseFeature = -> Chamfer013
  ChamferType = 0
  FlipDirection = false
  Placement = pos=(0,0,0) rot=(0.57735,0.57735,0.57735;2.0944rad)
  Size = 0.5
  Size2 = 1
  SupportTransform = false
FEATURE [PartDesign::Body] Body007  label="Joining bar"
  Group = -> [Sketch027,Pad010,Sketch028,Pad011,Mirrored007,Sketch029,Pocket015,Mirrored008,Fillet003,Chamfer013,Chamfer014]
  Origin = -> Origin011
  Placement = pos=(56,0,0) rot=(0,0,1;0rad)
  Tip = -> Chamfer014
FEATURE [Sketcher::SketchObject] Sketch030  label="LED guide tube spec"
  ExternalGeometry = -> [Chamfer012]
  FullyConstrained = false
  MapMode = 5
  Placement = pos=(0,-1e-16,0) rot=(-1,0,0;1.5708rad)
  Support = -> [Chamfer012]
  sketch-geometry (3):
    g0: Circle CenterX=-12.4 CenterY=-34 CenterZ=0 NormalX=0 NormalY=0 NormalZ=1 AngleXU=0 Radius=2.65
    g1: Circle CenterX=-12.4 CenterY=-34 CenterZ=0 NormalX=0 NormalY=0 NormalZ=1 AngleXU=0 Radius=5.15
    g2: LineSegment StartX=-9.75 StartY=-34 StartZ=0 EndX=-7.25 EndY=-34 EndZ=0
  constraints (7):
    c: Coincident(g0,g1)
    c: Coincident(g0,g-3)
    c: Equal(g0,g-3)
    c: Horizontal(g2)
    c: Perpendicular(g2,g0) = 1.5708
    c: PointOnObject(g2,g1)
    c: Distance(g2) = 2.5
FEATURE [PartDesign::Pad] Pad012  label="Add LED Guide Tube"
  AllowMultiFace = false
  BaseFeature = -> Chamfer012
  Direction = (1,1,1)
  Length = 4
  Length2 = 100
  Placement = pos=(0,0,0) rot=(1,0,0;1.5708rad)
  Profile = -> Sketch030
  Type = 0
FEATURE [Sketcher::SketchObject] Sketch031  label="LED Guide tube splitter tool"
  ExternalGeometry = -> [Pad012]
  FullyConstrained = false
  MapMode = 5
  Placement = pos=(0,4,-9e-16) rot=(-1,0,0;1.5708rad)
  Support = -> [Pad012]
  sketch-geometry (5):
    g0: LineSegment StartX=-17.55 StartY=-33 StartZ=0 EndX=-7.25 EndY=-33 EndZ=0
    g1: LineSegment StartX=-7.25 StartY=-33 StartZ=0 EndX=-7.25 EndY=-35 EndZ=0
    g2: LineSegment StartX=-7.25 StartY=-35 StartZ=0 EndX=-17.55 EndY=-35 EndZ=0
    g3: LineSegment StartX=-17.55 StartY=-35 StartZ=0 EndX=-17.55 EndY=-33 EndZ=0
    g4: LineSegment StartX=-17.55 StartY=-34 StartZ=0 EndX=-7.25 EndY=-34 EndZ=0
  constraints (14):
    c: Coincident(g0,g1)
    c: Coincident(g1,g2)
    c: Coincident(g2,g3)
    c: Coincident(g3,g0)
    c: Horizontal(g0)
    c: Horizontal(g2)
    c: Vertical(g1)
    c: Tangent(g1,g-3)
    c: Tangent(g3,g-3)
    c: Distance(g1) = 2
    c: Perpendicular(g4,g3) = 1.5708
    c: Perpendicular(g4,g1) = 4.71239
    c: Symmetric(g1,g0,g4)
    c: PointOnObject(g-3,g4)
FEATURE [PartDesign::Pocket] Pocket016  label="Split guide tube"
  AllowMultiFace = false
  BaseFeature = -> Pad012
  Length = 0
  Length2 = 100
  Placement = pos=(0,0,0) rot=(1,0,0;1.5708rad)
  Profile = -> Sketch031
  Type = 3
  UpToFace = -> Pad012 [Face3]
FEATURE [PartDesign::Pocket] Pocket017  label="Add PCB Screwholes"
  AllowMultiFace = false
  BaseFeature = -> Pad005
  Length = 5
  Length2 = 100
  Profile = -> Sketch010
  Type = 1
FEATURE [PartDesign::Chamfer] Chamfer015
  Angle = 45
  Base = -> Pocket017 [Edge6,Edge9]
  BaseFeature = -> Pocket017
  ChamferType = 0
  FlipDirection = false
  Size = 1
  Size2 = 1
  SupportTransform = false
FEATURE [PartDesign::Body] Body001  label="Base plate"
  Group = -> [Sketch001,Pad,Sketch009,Pad005,Sketch010,Pocket017,Chamfer015]
  Origin = -> Origin005
  Tip = -> Chamfer015
FEATURE [Sketcher::SketchObject] Sketch032
  FullyConstrained = true
  MapMode = 5
  Placement = pos=(-60,0,0) rot=(0.707107,0,0.707107;3.14159rad)
  Support = -> [Chamfer006]
  sketch-geometry (4):
    g0: ArcOfCircle CenterX=55 CenterY=32.5 CenterZ=0 NormalX=0 NormalY=0 NormalZ=1 AngleXU=0 Radius=1.5 StartAngle=5.59e-14 EndAngle=3.14159
    g1: ArcOfCircle CenterX=55 CenterY=-32.5 CenterZ=0 NormalX=0 NormalY=0 NormalZ=1 AngleXU=0 Radius=1.5 StartAngle=3.14159 EndAngle=6.28319
    g2: LineSegment StartX=53.5 StartY=32.5 StartZ=0 EndX=53.5 EndY=-32.5 EndZ=0
    g3: LineSegment StartX=56.5 StartY=32.5 StartZ=0 EndX=56.5 EndY=-32.5 EndZ=0
  constraints (9):
    c: Tangent(g0,g3) = 1.5708
    c: Tangent(g0,g2) = -1.5708
    c: Tangent(g2,g1) = -1.5708
    c: Tangent(g3,g1) = 1.5708
    c: Vertical(g2)
    c: Distance(g1,g1) = 3
    c: DistanceX(g1) = 55
    c: Symmetric(g1,g0,g-1)
    c: Distance(g3) = 65
FEATURE [PartDesign::Pad] Pad013
  AllowMultiFace = false
  BaseFeature = -> Chamfer006
  Direction = (1,1,1)
  Length = 4
  Length2 = 100
  Placement = pos=(0,0,0) rot=(1,0,0;1.5708rad)
  Profile = -> Sketch032
  Type = 0
FEATURE [Sketcher::SketchObject] Sketch033  label="Hoop profile"
  FullyConstrained = false
  MapMode = 5
  Support = -> [XY_Plane012]
  sketch-geometry (3):
    g0: Circle CenterX=0 CenterY=0 CenterZ=0 NormalX=0 NormalY=0 NormalZ=1 AngleXU=0 Radius=6.75
    g1: Circle CenterX=0 CenterY=0 CenterZ=0 NormalX=0 NormalY=0 NormalZ=1 AngleXU=0 Radius=8.2
    g2: LineSegment StartX=-8.2 StartY=1.2e-15 StartZ=0 EndX=-6.75 EndY=1.2e-15 EndZ=0
  constraints (7):
    c: Coincident(g0,g-1)
    c: Radius(g0) = 6.75
    c: Coincident(g1,g0)
    c: Perpendicular(g2,g0) = 4.71239
    c: Horizontal(g2)
    c: Perpendicular(g2,g1) = 4.71239
    c: Distance(g2) = 1.45
FEATURE [PartDesign::Pad] Pad014  label="Make hoop"
  AllowMultiFace = false
  Direction = (1,1,1)
  Length = 1.75
  Length2 = 100
  Profile = -> Sketch033
  Type = 0
FEATURE [Sketcher::SketchObject] Sketch034  label="Panel stiffeners"
  FullyConstrained = false
  MapMode = 5
  Placement = pos=(0,-1e-16,0) rot=(-1,0,0;1.5708rad)
  Support = -> [Mirrored006]
  sketch-geometry (8):
    g0: ArcOfCircle CenterX=-22.5 CenterY=-6 CenterZ=0 NormalX=0 NormalY=0 NormalZ=1 AngleXU=0 Radius=1.5 StartAngle=1.5708 EndAngle=4.71239
    g1: ArcOfCircle CenterX=22.5 CenterY=-6 CenterZ=0 NormalX=0 NormalY=0 NormalZ=1 AngleXU=0 Radius=1.5 StartAngle=4.71239 EndAngle=7.85398
    g2: LineSegment StartX=-22.5 StartY=-7.5 StartZ=0 EndX=22.5 EndY=-7.5 EndZ=0
    g3: LineSegment StartX=-22.5 StartY=-4.5 StartZ=0 EndX=22.5 EndY=-4.5 EndZ=0
    g4: ArcOfCircle CenterX=-47.5 CenterY=-35 CenterZ=0 NormalX=0 NormalY=0 NormalZ=1 AngleXU=0 Radius=1.5 StartAngle=1.5708 EndAngle=4.71239
    g5: ArcOfCircle CenterX=47.5 CenterY=-35 CenterZ=0 NormalX=0 NormalY=0 NormalZ=1 AngleXU=0 Radius=1.5 StartAngle=4.71239 EndAngle=7.85398
    g6: LineSegment StartX=-47.5 StartY=-36.5 StartZ=0 EndX=47.5 EndY=-36.5 EndZ=0
    g7: LineSegment StartX=-47.5 StartY=-33.5 StartZ=0 EndX=47.5 EndY=-33.5 EndZ=0
  constraints (18):
    c: Tangent(g0,g3) = 1.5708
    c: Tangent(g0,g2) = -1.5708
    c: Tangent(g2,g1) = -1.5708
    c: Tangent(g3,g1) = 1.5708
    c: Horizontal(g2)
    c: Tangent(g4,g7) = 1.5708
    c: Tangent(g4,g6) = -1.5708
    c: Tangent(g6,g5) = -1.5708
    c: Tangent(g7,g5) = 1.5708
    c: Horizontal(g6)
    c: Symmetric(g4,g5,g-2)
    c: Distance(g4,g4) = 3
    c: Distance(g5,g4) = 95
    c: DistanceY(g4) = -35
    c: Symmetric(g0,g1,g-2)
    c: Distance(g1,g1) = 3
    c: Distance(g1,g0) = 45
    c: DistanceY(g0) = -6
FEATURE [PartDesign::Pad] Pad015  label="Add panel stiffeners"
  AllowMultiFace = false
  BaseFeature = -> Mirrored006
  Direction = (1,1,1)
  Length = 2
  Length2 = 100
  Placement = pos=(0,0,0) rot=(1,0,0;1.5708rad)
  Profile = -> Sketch034
  Type = 0
FEATURE [PartDesign::Body] Body005  label="Rear Endplate"
  Group = -> [Sketch018,Pad008,Sketch019,Pad009,Mirrored004,Sketch020,Pocket009,Sketch021,Pocket010,Sketch022,Pocket011,Chamfer002,Chamfer007,Chamfer009,Mirrored006,Sketch034,Pad015]
  Origin = -> Origin009
  Placement = pos=(0,66.95,0) rot=(0,0,1;3.14159rad)
  Tip = -> Pad015
FEATURE [Sketcher::SketchObject] Sketch035  label="Stiffening bars for front plate"
  FullyConstrained = false
  MapMode = 5
  Placement = pos=(0,-1e-16,0) rot=(-1,0,0;1.5708rad)
  Support = -> [Pocket016]
  sketch-geometry (8):
    g0: ArcOfCircle CenterX=-40 CenterY=-55 CenterZ=0 NormalX=0 NormalY=0 NormalZ=1 AngleXU=0 Radius=1.5 StartAngle=1.5708 EndAngle=4.71239
    g1: ArcOfCircle CenterX=40 CenterY=-55 CenterZ=0 NormalX=0 NormalY=0 NormalZ=1 AngleXU=0 Radius=1.5 StartAngle=4.71239 EndAngle=7.85398
    g2: LineSegment StartX=-40 StartY=-56.5 StartZ=0 EndX=40 EndY=-56.5 EndZ=0
    g3: LineSegment StartX=-40 StartY=-53.5 StartZ=0 EndX=40 EndY=-53.5 EndZ=0
    g4: ArcOfCircle CenterX=-40 CenterY=-12 CenterZ=0 NormalX=0 NormalY=0 NormalZ=1 AngleXU=0 Radius=1.5 StartAngle=1.5708 EndAngle=4.71239
    g5: ArcOfCircle CenterX=40 CenterY=-12 CenterZ=0 NormalX=0 NormalY=0 NormalZ=1 AngleXU=0 Radius=1.5 StartAngle=4.71239 EndAngle=7.85398
    g6: LineSegment StartX=-40 StartY=-13.5 StartZ=0 EndX=40 EndY=-13.5 EndZ=0
    g7: LineSegment StartX=-40 StartY=-10.5 StartZ=0 EndX=40 EndY=-10.5 EndZ=0
  constraints (18):
    c: Tangent(g0,g3) = 1.5708
    c: Tangent(g0,g2) = -1.5708
    c: Tangent(g2,g1) = -1.5708
    c: Tangent(g3,g1) = 1.5708
    c: Horizontal(g2)
    c: Tangent(g4,g7) = 1.5708
    c: Tangent(g4,g6) = -1.5708
    c: Tangent(g6,g5) = -1.5708
    c: Tangent(g7,g5) = 1.5708
    c: Horizontal(g6)
    c: Equal(g3,g6)
    c: Distance(g5,g5) = 3
    c: Equal(g1,g5)
    c: Symmetric(g0,g1,g-2)
    c: Symmetric(g5,g4,g-2)
    c: DistanceY(g5) = -12
    c: DistanceY(g0) = -55
    c: Distance(g3) = 80
FEATURE [PartDesign::Pad] Pad016  label="Add stiffening bars to front plate"
  AllowMultiFace = false
  BaseFeature = -> Pocket016
  Direction = (1,1,1)
  Length = 4
  Length2 = 100
  Placement = pos=(0,0,0) rot=(1,0,0;1.5708rad)
  Profile = -> Sketch035
  Type = 0
FEATURE [PartDesign::Fillet] Fillet004
  Base = -> Pad016 [Face119]
  BaseFeature = -> Pad016
  Placement = pos=(0,0,0) rot=(1,0,0;1.5708rad)
  Radius = 0.1
  SupportTransform = false
FEATURE [PartDesign::Body] Body004  label="Front Endplate"
  Group = -> [Sketch011,Pad006,Sketch012,Pad007,Mirrored002,Sketch013,Pocket004,Sketch014,Pocket005,Chamfer004,Chamfer005,Chamfer008,Sketch024,Mirrored005,Pocket012,Sketch025,Pocket013,Chamfer010,Sketch026,Pocket014,Chamfer011,Chamfer012,Sketch030,Pad012,Sketch031,Pocket016,Sketch035,Pad016,Fillet004]
  Origin = -> Origin008
  Placement = pos=(0,-66.95,0) rot=(0,0,1;0rad)
  Tip = -> Fillet004
FEATURE [PartDesign::Chamfer] Chamfer016  label="Chamfer hoop"
  Angle = 45
  Base = -> Pad014 [Face4,Face3]
  BaseFeature = -> Pad014
  ChamferType = 0
  FlipDirection = false
  Size = 0.25
  Size2 = 1
  SupportTransform = false
FEATURE [PartDesign::Body] Body008  label="Hoop"
  Group = -> [Sketch033,Pad014,Chamfer016]
  Origin = -> Origin012
  Placement = pos=(-12.4,-68.6,34) rot=(0.999924,0.008726,-0.008726;1.57087rad)
  Tip = -> Chamfer016
FEATURE [Part::FeaturePython] Array005  label="Joining bar array"  # Draft array (typed FeaturePython)
  Angle = 360
  ArrayType = 1
  Axis = (0,0,1)
  Base = -> Body007
  Center = (0,0,0)
  Fuse = false
  IntervalAxis = (0,0,0)
  IntervalX = (1,0,0)
  IntervalY = (0,1,0)
  IntervalZ = (0,0,1)
  NumberPolar = 2
  NumberX = 2
  NumberY = 2
  NumberZ = 1
FEATURE [Sketcher::SketchObject] Sketch036  label="top cap profile"
  FullyConstrained = false
  MapMode = 5
  Support = -> [XY_Plane014]
  sketch-geometry (4):
    g0: LineSegment StartX=-63 StartY=70 StartZ=0 EndX=63 EndY=70 EndZ=0
    g1: LineSegment StartX=63 StartY=70 StartZ=0 EndX=63 EndY=-70 EndZ=0
    g2: LineSegment StartX=63 StartY=-70 StartZ=0 EndX=-63 EndY=-70 EndZ=0
    g3: LineSegment StartX=-63 StartY=-70 StartZ=0 EndX=-63 EndY=70 EndZ=0
  constraints (10):
    c: Coincident(g0,g1)
    c: Coincident(g1,g2)
    c: Coincident(g2,g3)
    c: Coincident(g3,g0)
    c: Horizontal(g2)
    c: Vertical(g1)
    c: Symmetric(g0,g0,g-2)
    c: Symmetric(g0,g2,g-1)
    c: Distance(g0) = 126
    c: Distance(g3) = 140
FEATURE [PartDesign::Pad] Pad017  label="Make top cap block"
  AllowMultiFace = false
  Direction = (1,1,1)
  Length = 43
  Length2 = 100
  Profile = -> Sketch036
  Type = 0
FEATURE [PartDesign::Thickness] Thickness  label="Turn block into a shell"
  Base = -> Pad017 [Face5]
  BaseFeature = -> Pad017
  Intersection = false
  Join = 1
  Mode = 0
  Reversed = true
  SupportTransform = false
  Value = 3
FEATURE [PartDesign::Chamfer] Chamfer017  label="Inner corner chamfers"
  Angle = 45
  Base = -> Thickness [Edge22,Edge24,Edge23,Edge17,Edge18,Edge19,Edge21,Edge20]
  BaseFeature = -> Thickness
  ChamferType = 0
  FlipDirection = false
  Size = 2
  Size2 = 1
  SupportTransform = false
FEATURE [Sketcher::SketchObject] Sketch037  label="Cap retaining holes spec"
  ExternalGeometry = -> [Chamfer017]
  FullyConstrained = false
  MapMode = 5
  Placement = pos=(-63,0,0) rot=(0.57735,-0.57735,-0.57735;2.0944rad)
  Support = -> [Chamfer017]
  sketch-geometry (2):
    g0: Circle CenterX=-45 CenterY=8 CenterZ=0 NormalX=0 NormalY=0 NormalZ=1 AngleXU=0 Radius=2.25
    g1: Circle CenterX=45 CenterY=8 CenterZ=0 NormalX=0 NormalY=0 NormalZ=1 AngleXU=0 Radius=2.25
  constraints (5):
    c: Symmetric(g0,g1,g-2)
    c: Radius(g0) = 2.25
    c: Equal(g0,g1)
    c: DistanceX(g-3,g0) = 25
    c: DistanceY(g-3,g0) = 8
FEATURE [PartDesign::Pocket] Pocket018  label="Add cap retaining screwholes"
  AllowMultiFace = false
  BaseFeature = -> Chamfer017
  Length = 5
  Length2 = 100
  Profile = -> Sketch037
  Type = 1
FEATURE [PartDesign::Chamfer] Chamfer018  label="Prettying chamfer"
  Angle = 45
  Base = -> Pocket018 [Face13,Face12,Face11,Face10]
  BaseFeature = -> Pocket018
  ChamferType = 0
  FlipDirection = false
  Size = 1
  Size2 = 1
  SupportTransform = false
FEATURE [Sketcher::SketchObject] Sketch038  label="Badge holding holes"
  ExternalGeometry = -> [Chamfer018]
  FullyConstrained = false
  MapMode = 5
  Placement = pos=(0,-70,0) rot=(1,0,0;1.5708rad)
  Support = -> [Chamfer018]
  sketch-geometry (3):
    g0: Circle CenterX=-20 CenterY=21.5 CenterZ=0 NormalX=0 NormalY=0 NormalZ=1 AngleXU=0 Radius=3.3
    g1: Circle CenterX=20 CenterY=21.5 CenterZ=0 NormalX=0 NormalY=0 NormalZ=1 AngleXU=0 Radius=3.3
    g2: LineSegment StartX=-23.3 StartY=21.5 StartZ=0 EndX=-62 EndY=21.5 EndZ=0
  constraints (7):
    c: Radius(g0) = 3.3
    c: Equal(g0,g1)
    c: Distance(g0,g1) = 40
    c: Symmetric(g0,g1,g-2)
    c: Perpendicular(g2,g0) = 1.5708
    c: Perpendicular(g2,g-3) = 4.71239
    c: Symmetric(g-3,g-3,g2)
FEATURE [PartDesign::Pocket] Pocket019  label="Add badge holding holes"
  AllowMultiFace = false
  BaseFeature = -> Chamfer018
  Length = 5
  Length2 = 100
  Profile = -> Sketch038
  Type = 0
FEATURE [PartDesign::Chamfer] Chamfer019  label="Chamfer badge holding holes"
  Angle = 45
  Base = -> Pocket019 [Face35,Face34]
  BaseFeature = -> Pocket019
  ChamferType = 0
  FlipDirection = false
  Size = 0.3
  Size2 = 1
  SupportTransform = false
FEATURE [Sketcher::SketchObject] Sketch039  label="Handle hole spec"
  FullyConstrained = false
  MapMode = 5
  Placement = pos=(0,0,40) rot=(1,0,0;3.14159rad)
  Support = -> [Chamfer019]
  sketch-geometry (2):
    g0: Circle CenterX=0 CenterY=48 CenterZ=0 NormalX=0 NormalY=0 NormalZ=1 AngleXU=0 Radius=2.3
    g1: Circle CenterX=0 CenterY=-48 CenterZ=0 NormalX=0 NormalY=0 NormalZ=1 AngleXU=0 Radius=2.3
  constraints (5):
    c: Symmetric(g1,g0,g-1)
    c: PointOnObject(g0,g-2)
    c: Distance(g0,g1) = 96
    c: Radius(g0) = 2.3
    c: Equal(g0,g1)
FEATURE [PartDesign::Pocket] Pocket020  label="Add handle holes"
  AllowMultiFace = false
  BaseFeature = -> Chamfer019
  Length = 5
  Length2 = 100
  Profile = -> Sketch039
  Type = 1
FEATURE [PartDesign::Chamfer] Chamfer020  label="Tidy handle holes"
  Angle = 45
  Base = -> Pocket020 [Face41,Face40]
  BaseFeature = -> Pocket020
  ChamferType = 0
  FlipDirection = false
  Size = 0.25
  Size2 = 1
  SupportTransform = false
FEATURE [PartDesign::Body] Body009  label="Cap"
  Group = -> [Sketch036,Pad017,Thickness,Chamfer017,Sketch037,Pocket018,Chamfer018,Sketch038,Pocket019,Chamfer019,Sketch039,Pocket020,Chamfer020]
  Origin = -> Origin014
  Tip = -> Chamfer020
FEATURE [App::Part] Part003  label="Final top cap assembly"
  Group = -> [Body009]
  Origin = -> Origin016
  Placement = pos=(-87.65,0,70) rot=(0.57735,0.57735,-0.57735;4.18879rad)
FEATURE [App::DocumentObjectGroup] Group003  label="Side Assemblies"
  Group = -> [Part,Part001,Part__Mirroring,Part__Mirroring004,Part__Mirroring003]
FEATURE [Sketcher::SketchObject] Sketch  label="Base tray footprint"
  FullyConstrained = true
  MapMode = 5
  Support = -> [XY_Plane]
  sketch-geometry (4):
    g0: LineSegment StartX=-60 StartY=87.5 StartZ=0 EndX=60 EndY=87.5 EndZ=0
    g1: LineSegment StartX=60 StartY=87.5 StartZ=0 EndX=60 EndY=-87.5 EndZ=0
    g2: LineSegment StartX=60 StartY=-87.5 StartZ=0 EndX=-60 EndY=-87.5 EndZ=0
    g3: LineSegment StartX=-60 StartY=-87.5 StartZ=0 EndX=-60 EndY=87.5 EndZ=0
  constraints (10):
    c: Coincident(g0,g1)
    c: Coincident(g1,g2)
    c: Coincident(g2,g3)
    c: Coincident(g3,g0)
    c: Horizontal(g2)
    c: Vertical(g1)
    c: Symmetric(g0,g0,g-2)
    c: Symmetric(g0,g2,g-1)
    c: Distance(g0) = 120
    c: Distance(g3) = 175
FEATURE [PartDesign::Pad] Pad018  label="Make Basetray"
  Direction = (1,1,1)
  Length = 17
  Length2 = 100
  Profile = -> Sketch
  Type = 0
FEATURE [Sketcher::SketchObject] Sketch042  label="Base Tray Hole pattern"
  ExternalGeometry = -> [Pad018]
  FullyConstrained = true
  MapMode = 5
  Placement = pos=(0,0,17) rot=(0,0,1;0rad)
  Support = -> [Pad018]
  sketch-geometry (11):
    g0: Circle CenterX=-39.425 CenterY=-81.1382 CenterZ=0 NormalX=0 NormalY=0 NormalZ=1 AngleXU=0 Radius=2.2
    g1: Circle CenterX=-39.425 CenterY=-30.2682 CenterZ=0 NormalX=0 NormalY=0 NormalZ=1 AngleXU=0 Radius=2.2
    g2: Circle CenterX=-39.425 CenterY=20.6018 CenterZ=0 NormalX=0 NormalY=0 NormalZ=1 AngleXU=0 Radius=2.2
    g3: Circle CenterX=-39.425 CenterY=72.7458 CenterZ=0 NormalX=0 NormalY=0 NormalZ=1 AngleXU=0 Radius=2.2
    g4: Circle CenterX=39.425 CenterY=72.7458 CenterZ=0 NormalX=0 NormalY=0 NormalZ=1 AngleXU=0 Radius=2.2
    g5: Circle CenterX=39.425 CenterY=20.6018 CenterZ=0 NormalX=0 NormalY=0 NormalZ=1 AngleXU=0 Radius=2.2
    g6: Circle CenterX=39.425 CenterY=-30.2682 CenterZ=0 NormalX=0 NormalY=0 NormalZ=1 AngleXU=0 Radius=2.2
    g7: Circle CenterX=39.425 CenterY=-81.1382 CenterZ=0 NormalX=0 NormalY=0 NormalZ=1 AngleXU=0 Radius=2.2
    g8: LineSegment StartX=-39.425 StartY=-81.1382 StartZ=0 EndX=-39.425 EndY=-30.2682 EndZ=0
    g9: LineSegment StartX=-39.425 StartY=-30.2682 StartZ=0 EndX=-39.425 EndY=20.6018 EndZ=0
    g10: LineSegment StartX=-39.425 StartY=20.6018 StartZ=0 EndX=-39.425 EndY=72.7458 EndZ=0
  constraints (26):
    c: Radius(g0) = 2.2
    c: Equal(g0,g7)
    c: Equal(g0,g1)
    c: Equal(g0,g6)
    c: Equal(g0,g5)
    c: Equal(g0,g2)
    c: Equal(g0,g3)
    c: Equal(g0,g4)
    c: Symmetric(g3,g4,g-2)
    c: Symmetric(g2,g5,g-2)
    c: Symmetric(g1,g6,g-2)
    c: Symmetric(g0,g7,g-2)
    c: Coincident(g8,g9)
    c: Coincident(g9,g10)
    c: Coincident(g10,g3)
    c: Coincident(g9,g2)
    c: Coincident(g8,g1)
    c: Coincident(g0,g8)
    c: DistanceY(g-3,g0) = 6.3618
    c: DistanceX(g0,g7) = 78.85
    c: Vertical(g8)
    c: Vertical(g9)
    c: Vertical(g10)
    c: Distance(g8) = 50.87
    c: Distance(g9) = 50.87
    c: Distance(g10) = 52.144
FEATURE [PartDesign::Pocket] Pocket021  label="Make PCB Mounting Holes"
  BaseFeature = -> Pad018
  Length = 5
  Length2 = 100
  Profile = -> Sketch042
  Type = 1
FEATURE [Sketcher::SketchObject] Sketch043  label="Center space cutout spec for PCB"
  ExternalGeometry = -> [Pocket021]
  FullyConstrained = true
  MapMode = 5
  Placement = pos=(0,-87.5,0) rot=(1,0,0;1.5708rad)
  Support = -> [Pocket021]
  sketch-geometry (4):
    g0: LineSegment StartX=-50.5 StartY=17 StartZ=0 EndX=50.5 EndY=17 EndZ=0
    g1: LineSegment StartX=50.5 StartY=17 StartZ=0 EndX=50.5 EndY=3 EndZ=0
    g2: LineSegment StartX=50.5 StartY=3 StartZ=0 EndX=-50.5 EndY=3 EndZ=0
    g3: LineSegment StartX=-50.5 StartY=3 StartZ=0 EndX=-50.5 EndY=17 EndZ=0
  constraints (11):
    c: Coincident(g0,g1)
    c: Coincident(g1,g2)
    c: Coincident(g2,g3)
    c: Coincident(g3,g0)
    c: Horizontal(g0)
    c: Vertical(g1)
    c: Vertical(g3)
    c: DistanceY(g-3,g1) = 3
    c: Symmetric(g2,g1,g-2)
    c: DistanceX(g1,g-3) = 9.5
    c: PointOnObject(g0,g-4)
FEATURE [PartDesign::Pocket] Pocket022  label="Make center space for PCB"
  BaseFeature = -> Pocket021
  Length = 5
  Length2 = 100
  Profile = -> Sketch043
  Type = 1
FEATURE [Sketcher::SketchObject] Sketch044  label="Side panel screwhole spec"
  FullyConstrained = true
  MapMode = 5
  Placement = pos=(-60,0,0) rot=(0.57735,-0.57735,-0.57735;2.0944rad)
  Support = -> [Pocket022]
  sketch-geometry (7):
    g0: Circle CenterX=75 CenterY=10.5 CenterZ=0 NormalX=0 NormalY=0 NormalZ=1 AngleXU=0 Radius=2.2
    g1: Circle CenterX=25 CenterY=10.5 CenterZ=0 NormalX=0 NormalY=0 NormalZ=1 AngleXU=0 Radius=2.2
    g2: Circle CenterX=-25 CenterY=10.5 CenterZ=0 NormalX=0 NormalY=0 NormalZ=1 AngleXU=0 Radius=2.2
    g3: Circle CenterX=-75 CenterY=10.5 CenterZ=0 NormalX=0 NormalY=0 NormalZ=1 AngleXU=0 Radius=2.2
    g4: LineSegment StartX=75 StartY=10.5 StartZ=0 EndX=25 EndY=10.5 EndZ=0
    g5: LineSegment StartX=25 StartY=10.5 StartZ=0 EndX=-25 EndY=10.5 EndZ=0
    g6: LineSegment StartX=-25 StartY=10.5 StartZ=0 EndX=-75 EndY=10.5 EndZ=0
  constraints (17):
    c: Coincident(g4,g5)
    c: Coincident(g5,g6)
    c: Equal(g6,g5)
    c: Equal(g5,g4)
    c: Horizontal(g6)
    c: Horizontal(g4)
    c: Coincident(g6,g3)
    c: Coincident(g5,g2)
    c: Coincident(g4,g1)
    c: Coincident(g4,g0)
    c: Distance(g4) = 50
    c: DistanceY(g0) = 10.5
    c: Symmetric(g3,g0,g-2)
    c: Radius(g3) = 2.2
    c: Equal(g3,g2)
    c: Equal(g3,g1)
    c: Equal(g3,g0)
FEATURE [PartDesign::Pocket] Pocket023  label="Add side panel screwholes"
  BaseFeature = -> Pocket022
  Length = 5
  Length2 = 100
  Profile = -> Sketch044
  Type = 1
FEATURE [Sketcher::SketchObject] Sketch045  label="Nut trap pocket spec"
  ExternalGeometry = -> [Pocket023]
  FullyConstrained = true
  MapMode = 5
  Placement = pos=(0,0,17) rot=(0,0,1;0rad)
  Support = -> [Pocket023]
  sketch-geometry (18):
    g0: LineSegment StartX=-57 StartY=28.5 StartZ=0 EndX=-53.5 EndY=28.5 EndZ=0
    g1: LineSegment StartX=-53.5 StartY=28.5 StartZ=0 EndX=-53.5 EndY=21.5 EndZ=0
    g2: LineSegment StartX=-53.5 StartY=21.5 StartZ=0 EndX=-57 EndY=21.5 EndZ=0
    g3: LineSegment StartX=-57 StartY=21.5 StartZ=0 EndX=-57 EndY=28.5 EndZ=0
    g4: LineSegment StartX=-57 StartY=-21.5 StartZ=0 EndX=-53.5 EndY=-21.5 EndZ=0
    g5: LineSegment StartX=-53.5 StartY=-21.5 StartZ=0 EndX=-53.5 EndY=-28.5 EndZ=0
    g6: LineSegment StartX=-53.5 StartY=-28.5 StartZ=0 EndX=-57 EndY=-28.5 EndZ=0
    g7: LineSegment StartX=-57 StartY=-28.5 StartZ=0 EndX=-57 EndY=-21.5 EndZ=0
    g8: LineSegment StartX=-57 StartY=-71.5 StartZ=0 EndX=-53.5 EndY=-71.5 EndZ=0
    g9: LineSegment StartX=-53.5 StartY=-71.5 StartZ=0 EndX=-53.5 EndY=-78.5 EndZ=0
    g10: LineSegment StartX=-53.5 StartY=-78.5 StartZ=0 EndX=-57 EndY=-78.5 EndZ=0
    g11: LineSegment StartX=-57 StartY=-78.5 StartZ=0 EndX=-57 EndY=-71.5 EndZ=0
    g12: LineSegment StartX=-57 StartY=78.5 StartZ=0 EndX=-53.5 EndY=78.5 EndZ=0
    g13: LineSegment StartX=-53.5 StartY=78.5 StartZ=0 EndX=-53.5 EndY=71.5 EndZ=0
    g14: LineSegment StartX=-53.5 StartY=71.5 StartZ=0 EndX=-57 EndY=71.5 EndZ=0
    g15: LineSegment StartX=-57 StartY=71.5 StartZ=0 EndX=-57 EndY=78.5 EndZ=0
    g16: LineSegment StartX=-55.25 StartY=87.5 StartZ=0 EndX=-55.25 EndY=78.5 EndZ=0
    g17: LineSegment StartX=-53.5 StartY=71.5 StartZ=0 EndX=-53.5 EndY=28.5 EndZ=0
  constraints (50):
    c: Coincident(g0,g1)
    c: Coincident(g1,g2)
    c: Coincident(g2,g3)
    c: Coincident(g3,g0)
    c: Horizontal(g0)
    c: Horizontal(g2)
    c: Vertical(g1)
    c: Vertical(g3)
    c: Coincident(g4,g5)
    c: Coincident(g5,g6)
    c: Coincident(g6,g7)
    c: Coincident(g7,g4)
    c: Horizontal(g4)
    c: Horizontal(g6)
    c: Vertical(g5)
    c: Vertical(g7)
    c: Coincident(g8,g9)
    c: Coincident(g9,g10)
    c: Coincident(g10,g11)
    c: Coincident(g11,g8)
    c: Horizontal(g8)
    c: Horizontal(g10)
    c: Vertical(g9)
    c: Vertical(g11)
    c: Coincident(g12,g13)
    c: Coincident(g13,g14)
    c: Coincident(g14,g15)
    c: Coincident(g15,g12)
    c: Horizontal(g14)
    c: Vertical(g13)
    c: Vertical(g15)
    c: Equal(g12,g0)
    c: Equal(g0,g4)
    c: Equal(g4,g8)
    c: Equal(g9,g5)
    c: Equal(g5,g13)
    c: Equal(g13,g1)
    c: Distance(g13) = 7
    c: Distance(g12) = 3.5
    c: Symmetric(g-3,g-3,g16)
    c: PointOnObject(g16,g-3)
    c: DistanceY(g0,g12) = 50
    c: Symmetric(g0,g5,g-1)
    c: DistanceY(g5,g1) = 50
    c: Coincident(g17,g13)
    c: Coincident(g17,g0)
    c: Vertical(g17)
    c: Symmetric(g12,g9,g-1)
    c: PointOnObject(g16,g12)
    c: Symmetric(g12,g12,g16)
FEATURE [PartDesign::Pocket] Pocket024  label="Add nut trap pockets"
  BaseFeature = -> Pocket023
  Length = 10.7
  Length2 = 100
  Profile = -> Sketch045
  Type = 0
FEATURE [PartDesign::Mirrored] Mirrored009  label="Add nut trap pockets to other side"
  BaseFeature = -> Pocket024
  MirrorPlane = -> Sketch045 [V_Axis]
  Originals = -> [Pocket024]
FEATURE [Sketcher::SketchObject] Sketch046  label="Waste material trim tool"
  ExternalGeometry = -> [Mirrored009]
  FullyConstrained = true
  MapMode = 5
  Placement = pos=(0,0,17) rot=(0,0,1;0rad)
  Support = -> [Mirrored009]
  sketch-geometry (20):
    g0: LineSegment StartX=-57 StartY=-81.5 StartZ=0 EndX=-50.5 EndY=-81.5 EndZ=0
    g1: LineSegment StartX=-50.5 StartY=-81.5 StartZ=0 EndX=-50.5 EndY=-87.5 EndZ=0
    g2: LineSegment StartX=-50.5 StartY=-87.5 StartZ=0 EndX=-57 EndY=-87.5 EndZ=0
    g3: LineSegment StartX=-57 StartY=-87.5 StartZ=0 EndX=-57 EndY=-81.5 EndZ=0
    g4: LineSegment StartX=-57 StartY=87.5 StartZ=0 EndX=-50.5 EndY=87.5 EndZ=0
    g5: LineSegment StartX=-50.5 StartY=87.5 StartZ=0 EndX=-50.5 EndY=81.5 EndZ=0
    g6: LineSegment StartX=-50.5 StartY=81.5 StartZ=0 EndX=-57 EndY=81.5 EndZ=0
    g7: LineSegment StartX=-57 StartY=81.5 StartZ=0 EndX=-57 EndY=87.5 EndZ=0
    g8: LineSegment StartX=-57 StartY=68.5 StartZ=0 EndX=-50.5 EndY=68.5 EndZ=0
    g9: LineSegment StartX=-50.5 StartY=68.5 StartZ=0 EndX=-50.5 EndY=31.5 EndZ=0
    g10: LineSegment StartX=-50.5 StartY=31.5 StartZ=0 EndX=-57 EndY=31.5 EndZ=0
    g11: LineSegment StartX=-57 StartY=31.5 StartZ=0 EndX=-57 EndY=68.5 EndZ=0
    g12: LineSegment StartX=-57 StartY=-31.5 StartZ=0 EndX=-50.5 EndY=-31.5 EndZ=0
    g13: LineSegment StartX=-50.5 StartY=-31.5 StartZ=0 EndX=-50.5 EndY=-68.5 EndZ=0
    g14: LineSegment StartX=-50.5 StartY=-68.5 StartZ=0 EndX=-57 EndY=-68.5 EndZ=0
    g15: LineSegment StartX=-57 StartY=-68.5 StartZ=0 EndX=-57 EndY=-31.5 EndZ=0
    g16: LineSegment StartX=-57 StartY=18.5 StartZ=0 EndX=-50.5 EndY=18.5 EndZ=0
    g17: LineSegment StartX=-50.5 StartY=18.5 StartZ=0 EndX=-50.5 EndY=-18.5 EndZ=0
    g18: LineSegment StartX=-50.5 StartY=-18.5 StartZ=0 EndX=-57 EndY=-18.5 EndZ=0
    g19: LineSegment StartX=-57 StartY=-18.5 StartZ=0 EndX=-57 EndY=18.5 EndZ=0
  constraints (56):
    c: Coincident(g0,g1)
    c: Coincident(g1,g2)
    c: Coincident(g2,g3)
    c: Coincident(g3,g0)
    c: Horizontal(g0)
    c: Horizontal(g2)
    c: Vertical(g1)
    c: Vertical(g3)
    c: Coincident(g1,g-3)
    c: DistanceX(g-4,g2) = 3
    c: DistanceY(g0,g-5) = 3
    c: Coincident(g4,g5)
    c: Coincident(g5,g6)
    c: Coincident(g6,g7)
    c: Coincident(g7,g4)
    c: Horizontal(g4)
    c: Horizontal(g6)
    c: Vertical(g5)
    c: Vertical(g7)
    c: Coincident(g4,g-3)
    c: Equal(g5,g1)
    c: Equal(g0,g4)
    c: Coincident(g8,g9)
    c: Coincident(g9,g10)
    c: Coincident(g10,g11)
    c: Coincident(g11,g8)
    c: Horizontal(g8)
    c: Horizontal(g10)
    c: Vertical(g9)
    c: Vertical(g11)
    c: Coincident(g12,g13)
    c: Coincident(g13,g14)
    c: Coincident(g14,g15)
    c: Coincident(g15,g12)
    c: Horizontal(g12)
    c: Horizontal(g14)
    c: Vertical(g13)
    c: Vertical(g15)
    c: Equal(g8,g4)
    c: Equal(g4,g12)
    c: PointOnObject(g8,g-3)
    c: DistanceY(g-7,g10) = 3
    c: DistanceY(g8,g-6) = 3
    c: Equal(g11,g15)
    c: Symmetric(g12,g9,g-1)
    c: Coincident(g16,g17)
    c: Coincident(g17,g18)
    c: Coincident(g18,g19)
    c: Coincident(g19,g16)
    c: Horizontal(g16)
    c: Horizontal(g18)
    c: Vertical(g17)
    c: Equal(g18,g12)
    c: Equal(g17,g13)
    c: PointOnObject(g17,g-3)
    c: Symmetric(g16,g18,g-1)
FEATURE [PartDesign::Pocket] Pocket025  label="Trim waste material from side around nut traps"
  BaseFeature = -> Mirrored009
  Length = 0
  Length2 = 100
  Profile = -> Sketch046
  Type = 3
  UpToFace = -> Mirrored009 [Face6]
FEATURE [PartDesign::Mirrored] Mirrored010  label="Trim waste material from other side aound nut traps"
  BaseFeature = -> Pocket025
  MirrorPlane = -> Sketch046 [V_Axis]
  Originals = -> [Pocket025]
FEATURE [Sketcher::SketchObject] Sketch047  label="PCB Pillars spec"
  ExternalGeometry = -> [Mirrored010]
  FullyConstrained = true
  MapMode = 5
  Placement = pos=(0,7e-16,3) rot=(0,0,1;0rad)
  Support = -> [Mirrored010]
  sketch-geometry (9):
    g0: LineSegment StartX=-39.425 StartY=70.5458 StartZ=0 EndX=-39.425 EndY=68.0458 EndZ=0
    g1: Circle CenterX=-39.425 CenterY=-81.1382 CenterZ=0 NormalX=0 NormalY=0 NormalZ=1 AngleXU=0 Radius=2.2
    g2: Circle CenterX=-39.425 CenterY=-30.2682 CenterZ=0 NormalX=0 NormalY=0 NormalZ=1 AngleXU=0 Radius=2.2
    g3: Circle CenterX=-39.425 CenterY=20.6018 CenterZ=0 NormalX=0 NormalY=0 NormalZ=1 AngleXU=0 Radius=2.2
    g4: Circle CenterX=-39.425 CenterY=72.7458 CenterZ=0 NormalX=0 NormalY=0 NormalZ=1 AngleXU=0 Radius=2.2
    g5: Circle CenterX=-39.425 CenterY=72.7458 CenterZ=0 NormalX=0 NormalY=0 NormalZ=1 AngleXU=0 Radius=4.7
    g6: Circle CenterX=-39.425 CenterY=20.6018 CenterZ=0 NormalX=0 NormalY=0 NormalZ=1 AngleXU=0 Radius=4.7
    g7: Circle CenterX=-39.425 CenterY=-30.2682 CenterZ=0 NormalX=0 NormalY=0 NormalZ=1 AngleXU=0 Radius=4.7
    g8: Circle CenterX=-39.425 CenterY=-81.1382 CenterZ=0 NormalX=0 NormalY=0 NormalZ=1 AngleXU=0 Radius=4.7
  constraints (19):
    c: Vertical(g0)
    c: Distance(g0) = 2.5
    c: Coincident(g-3,g4)
    c: Coincident(g-4,g3)
    c: Coincident(g-5,g2)
    c: Coincident(g-6,g1)
    c: Equal(g1,g2)
    c: Equal(g2,g3)
    c: Equal(g3,g4)
    c: Equal(g4,g-3)
    c: Perpendicular(g0,g4) = 1.5708
    c: Coincident(g1,g8)
    c: Coincident(g2,g7)
    c: Coincident(g6,g3)
    c: PointOnObject(g0,g5)
    c: Coincident(g4,g5)
    c: Equal(g6,g5)
    c: Equal(g5,g7)
    c: Equal(g7,g8)
FEATURE [PartDesign::Pad] Pad019  label="Make PCB Pillars down one side"
  BaseFeature = -> Mirrored010
  Direction = (1,1,1)
  Length = 5
  Length2 = 100
  Profile = -> Sketch047
  Type = 0
FEATURE [PartDesign::Mirrored] Mirrored011  label="Add PCB Pillars to other side"
  BaseFeature = -> Pad019
  MirrorPlane = -> Sketch047 [V_Axis]
  Originals = -> [Pad019]
FEATURE [Part::Part2DObjectPython] ShapeString  label="Shapestring 'Top'"  # Draft 2D object (typed FeaturePython)
  FontFile = <userpath>/USERROOT/Fonts/impact.ttf
  Placement = pos=(-15,66,3) rot=(0,0,1;0rad)
  Size = 16
  String = Top
  Tracking = 0
FEATURE [PartDesign::Pocket] Pocket026  label="Add 'Top' to tray"
  BaseFeature = -> Mirrored011
  Length = 1.5
  Length2 = 100
  Profile = -> ShapeString
  Type = 0
FEATURE [PartDesign::Chamfer] Chamfer  label="Nut trap lead-in chamfer"
  Angle = 45
  Base = -> Pocket026 [Edge163,Edge164,Edge166,Edge165,Edge170,Edge168,Edge167,Edge169,Edge159,Edge160,Edge161,Edge162,Edge155,Edge156,Edge158,Edge157,Edge48,Edge47,Edge52,Edge51,Edge60,Edge59,Edge56,Edge55,Edge57,Edge54,Edge61,Edge58,Edge53,Edge50,Edge49,Edge46]
  BaseFeature = -> Pocket026
  ChamferType = 0
  FlipDirection = false
  Size = 0.5
  Size2 = 1
  SupportTransform = false
FEATURE [PartDesign::Chamfer] Chamfer021  label="Print aide bottom hole chamfers"
  Angle = 45
  Base = -> Pocket026 [Edge21,Edge20,Edge17,Edge16,Edge15,Edge14,Edge19,Edge18]
  BaseFeature = -> Pocket026
  ChamferType = 0
  FlipDirection = false
  Size = 0.5
  Size2 = 1
  SupportTransform = false
FEATURE [PartDesign::Body] Body  label="V3 Basetray"
  Group = -> [Sketch,Pad018,Sketch042,Pocket021,Sketch043,Pocket022,Sketch044,Pocket023,Sketch045,Pocket024,Mirrored009,Sketch046,Pocket025,Mirrored010,Sketch047,Pad019,Mirrored011,ShapeString,Pocket026,Chamfer,Chamfer021]
  Origin = -> Origin
  Placement = pos=(0,0,0) rot=(0,0,1;1.5708rad)
  Tip = -> Chamfer021
FEATURE [PartDesign::Chamfer] Chamfer022
  Angle = 45
  Base = -> Pad013 [Edge15,Edge11]
  BaseFeature = -> Pad013
  ChamferType = 0
  FlipDirection = false
  Placement = pos=(0,0,0) rot=(1,0,0;1.5708rad)
  Size = 1
  Size2 = 1
  SupportTransform = false
FEATURE [PartDesign::Body] Body002  label="LH Side plate"
  Group = -> [Sketch002,Pad001,Sketch003,Pad002,Mirrored,Sketch004,Pocket,Mirrored001,Sketch015,Pocket006,Mirrored003,Sketch016,Pocket007,Sketch017,Pocket008,LinearPattern,Chamfer001,Chamfer006,Sketch032,Pad013,Chamfer022]
  Origin = -> Origin006
  Tip = -> Chamfer022
FEATURE [Part::FeaturePython] Array003  label="Sideplate array"  # Draft array (typed FeaturePython)
  Angle = 360
  ArrayType = 1
  Axis = (0,0,1)
  Base = -> Body002
  Center = (0,0,0)
  Fuse = false
  IntervalAxis = (0,0,0)
  IntervalX = (1,0,0)
  IntervalY = (0,1,0)
  IntervalZ = (0,0,1)
  NumberPolar = 2
  NumberX = 2
  NumberY = 2
  NumberZ = 1
FEATURE [App::Part] Part002  label="Final bottom cap assembly"
  Group = -> [Body008,Body005,Array003,Body002,Array005,Body007,Array004,Body006,Body004,Body003,Body001]
  Origin = -> Origin013
  Placement = pos=(155.65,0,70) rot=(-0.57735,-0.57735,0.57735;2.0944rad)
FEATURE [App::DocumentObjectGroup] Group002  label="Endcaps"
  Group = -> [Part003,Part002]
FEATURE [App::Part] Part004  label="Entire Assembly"
  Group = -> [Part003,Part002,Part__Feature005,Array001,Part__Mirroring004,Part,Part001,Part__Feature006,Part__Mirroring,Part__Feature004,Array,Part__Mirroring003,Part__Feature001,Part__Mirroring001,Group002,Group003]
  Origin = -> Origin017
